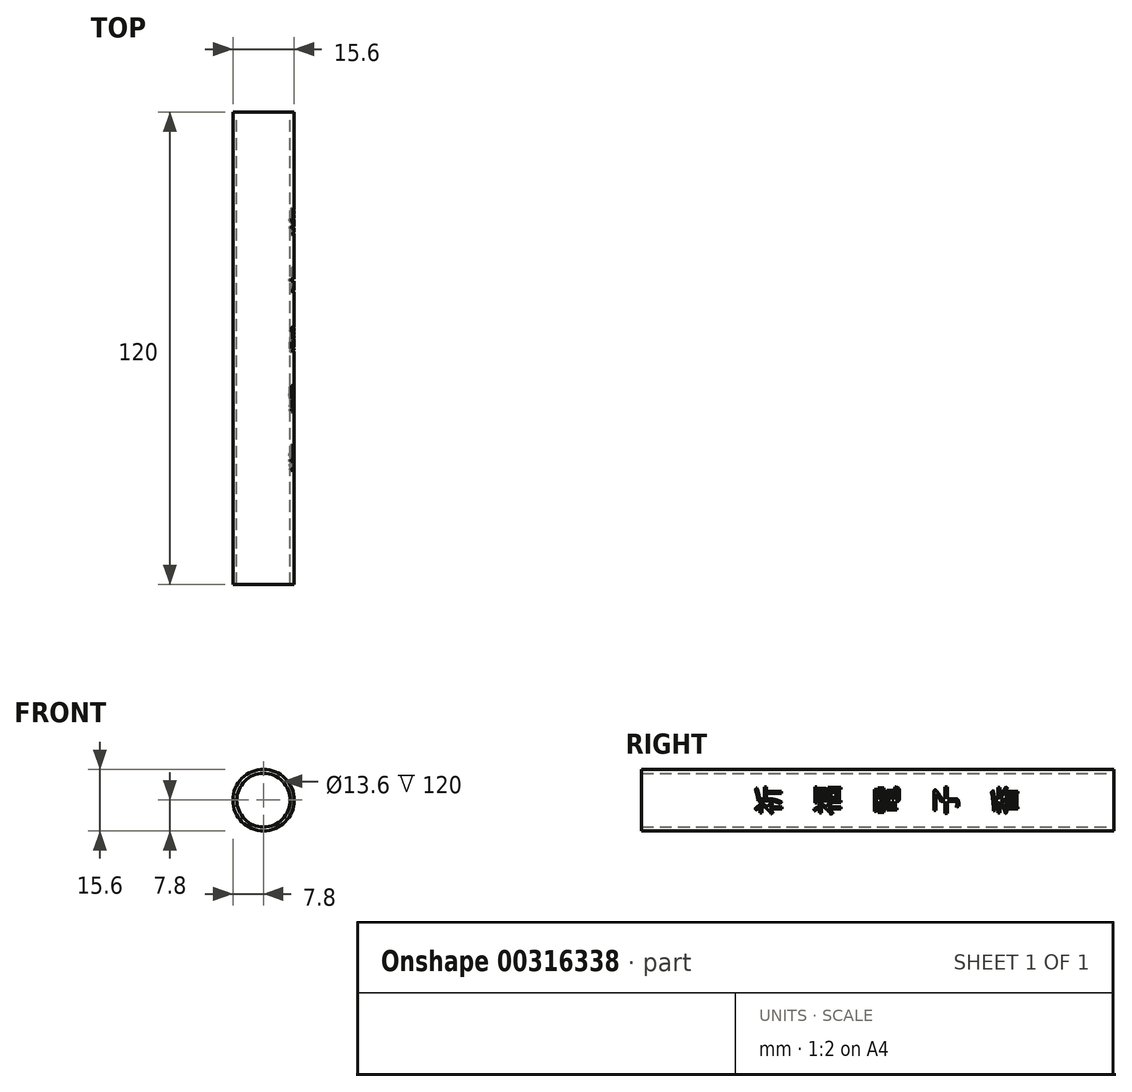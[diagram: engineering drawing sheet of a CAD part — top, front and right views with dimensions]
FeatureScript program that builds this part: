
annotation { "Feature Type Name" : "Feature", "Feature Type Description" : "" }
export const myFeature = defineFeature(function(context is Context, id is Id, definition is map)
    precondition{}
    {
        {
            var Q0;
            Q0=qCreatedBy(makeId("Front.planeOp"),FACE);
            var sketch = newSketch(context, id + "F0", { "sketchPlane" : qUnion([Q0])});
            skCircle(sketch, "E0", {"center": v(0, 0) * mm, "radius": 7.8 * mm});
            skSolve(sketch);
        }
        {
            var Q0;
            Q0 = qSketchRegion(id + "F0", true);
            extrude(context, id + "F1", {"entities" : qUnion([Q0]), "depth" : 120 * mm});
        }
        {
            var Q0;
            Q0=makeQuery(id+"F1.opExtrude","CAP_FACE",FACE,{"disambiguationData":[OSD([sQuery(id+"F0.wireOp",EDGE,"E0")])],"isStart":true});
            var sketch = newSketch(context, id + "F2", { "sketchPlane" : qUnion([Q0])});
            skCircle(sketch, "E1", {"center": v(0, 0) * mm, "radius": 6.8 * mm});
            skSolve(sketch);
        }
        {
            var Q0;
            Q0 = qSketchRegion(id + "F2", true);
            extrude(context, id + "F3", {"entities" : qUnion([Q0]), "operationType" : NewBodyOperationType.REMOVE, "oppositeDirection" : true, "depth" : 120 * mm});
        }
        {
            var Q0;
            Q0=qCreatedBy(makeId("Right.planeOp"),FACE);
            cPlane(context, id + "F4", {"entities" : qUnion([Q0]), "cplaneType" : CPlaneType.OFFSET, "offset" : 10 * mm, "width" : 150 * mm, "height" : 150 * mm});
        }
        {
            var Q0;
            Q0=qCreatedBy(id+"F4.planeOp",FACE);
            var sketch = newSketch(context, id + "F5", { "sketchPlane" : qUnion([Q0])});
            skText(sketch, "E2", { "text": "祈", "fontName": "NotoSansCJKtc-Regular.otf"});
            skText(sketch, "E3", { "text": "福", "fontName": "NotoSansCJKtc-Regular.otf"});
            skText(sketch, "E4", { "text": "電", "fontName": "NotoSansCJKtc-Regular.otf"});
            skText(sketch, "E5", { "text": "子", "fontName": "NotoSansCJKtc-Regular.otf"});
            skText(sketch, "E6", { "text": "香", "fontName": "NotoSansCJKtc-Regular.otf"});
            const initialGuessF5  = {"E2": [-0.085, -0.00375, 0, 1, 0.00534], "E3": [-0.07, -0.00375, 0, 1, 0.00543], "E4": [-0.055, -0.00375, 0, 1, 0.00532], "E5": [-0.04, -0.00375, 0, 1, 0.00537], "E6": [-0.025, -0.00375, 0, 1, 0.00536]};
            skSetInitialGuess(sketch, initialGuessF5);
            skSolve(sketch);
        }
        {
            var Q0;
            Q0 = qSketchRegion(id + "F5", true);
            var Q1;
            Q1=makeQuery(id+"F1.opExtrude","SWEPT_FACE",FACE,{"disambiguationData":[OSD([sQuery(id+"F0.wireOp",EDGE,"E0")])]});
            extrude(context, id + "F6", {"entities" : qUnion([Q0]), "endBound" : BoundingType.UP_TO_SURFACE, "oppositeDirection" : true, "endBoundEntityFace" : qUnion([Q1]), "depth" : 2 * mm});
        }
        {
            var Q0;
            Q0=makeQuery(id+"F6.opExtrude","SWEPT_BODY",BODY,{"disambiguationData":[OSD([sQuery(id+"F5.wireOp",EDGE,"E2.sketch_text.stroke-0"),sQuery(id+"F5.wireOp",EDGE,"E2.sketch_text.stroke-1"),sQuery(id+"F5.wireOp",EDGE,"E2.sketch_text.stroke-2"),sQuery(id+"F5.wireOp",EDGE,"E2.sketch_text.stroke-3")])]});
            var Q1;
            Q1=makeQuery(id+"F6.opExtrude","SWEPT_BODY",BODY,{"disambiguationData":[OSD([sQuery(id+"F5.wireOp",EDGE,"E2.sketch_text.stroke-4"),sQuery(id+"F5.wireOp",EDGE,"E2.sketch_text.stroke-5"),sQuery(id+"F5.wireOp",EDGE,"E2.sketch_text.stroke-6"),sQuery(id+"F5.wireOp",EDGE,"E2.sketch_text.stroke-7"),sQuery(id+"F5.wireOp",EDGE,"E2.sketch_text.stroke-8"),sQuery(id+"F5.wireOp",EDGE,"E2.sketch_text.stroke-9"),sQuery(id+"F5.wireOp",EDGE,"E2.sketch_text.stroke-10"),sQuery(id+"F5.wireOp",EDGE,"E2.sketch_text.stroke-11"),sQuery(id+"F5.wireOp",EDGE,"E2.sketch_text.stroke-12"),sQuery(id+"F5.wireOp",EDGE,"E2.sketch_text.stroke-13"),sQuery(id+"F5.wireOp",EDGE,"E2.sketch_text.stroke-14"),sQuery(id+"F5.wireOp",EDGE,"E2.sketch_text.stroke-15"),sQuery(id+"F5.wireOp",EDGE,"E2.sketch_text.stroke-16"),sQuery(id+"F5.wireOp",EDGE,"E2.sketch_text.stroke-17"),sQuery(id+"F5.wireOp",EDGE,"E2.sketch_text.stroke-18")])]});
            var Q2;
            Q2=makeQuery(id+"F6.opExtrude","SWEPT_BODY",BODY,{"disambiguationData":[OSD([sQuery(id+"F5.wireOp",EDGE,"E2.sketch_text.stroke-19"),sQuery(id+"F5.wireOp",EDGE,"E2.sketch_text.stroke-20"),sQuery(id+"F5.wireOp",EDGE,"E2.sketch_text.stroke-21"),sQuery(id+"F5.wireOp",EDGE,"E2.sketch_text.stroke-22"),sQuery(id+"F5.wireOp",EDGE,"E2.sketch_text.stroke-23"),sQuery(id+"F5.wireOp",EDGE,"E2.sketch_text.stroke-24"),sQuery(id+"F5.wireOp",EDGE,"E2.sketch_text.stroke-25"),sQuery(id+"F5.wireOp",EDGE,"E2.sketch_text.stroke-26"),sQuery(id+"F5.wireOp",EDGE,"E2.sketch_text.stroke-27"),sQuery(id+"F5.wireOp",EDGE,"E2.sketch_text.stroke-28"),sQuery(id+"F5.wireOp",EDGE,"E2.sketch_text.stroke-29"),sQuery(id+"F5.wireOp",EDGE,"E2.sketch_text.stroke-30"),sQuery(id+"F5.wireOp",EDGE,"E2.sketch_text.stroke-31"),sQuery(id+"F5.wireOp",EDGE,"E2.sketch_text.stroke-32"),sQuery(id+"F5.wireOp",EDGE,"E2.sketch_text.stroke-33")])]});
            transform(context, id + "F7", {"entities" : qUnion([Q0, Q1, Q2]), "transformType" : TransformType.TRANSLATION_3D, "dx" : 1 * mm, "dy" : 0 * mm, "dz" : 0 * mm, "makeCopy" : true});
        }
        {
            var Q0;
            Q0=makeQuery(id+"F7.opPattern","COPY",BODY,{"derivedFrom":makeQuery(id+"F6.opExtrude","SWEPT_BODY",BODY,{"disambiguationData":[OSD([sQuery(id+"F5.wireOp",EDGE,"E2.sketch_text.stroke-19"),sQuery(id+"F5.wireOp",EDGE,"E2.sketch_text.stroke-20"),sQuery(id+"F5.wireOp",EDGE,"E2.sketch_text.stroke-21"),sQuery(id+"F5.wireOp",EDGE,"E2.sketch_text.stroke-22"),sQuery(id+"F5.wireOp",EDGE,"E2.sketch_text.stroke-23"),sQuery(id+"F5.wireOp",EDGE,"E2.sketch_text.stroke-24"),sQuery(id+"F5.wireOp",EDGE,"E2.sketch_text.stroke-25"),sQuery(id+"F5.wireOp",EDGE,"E2.sketch_text.stroke-26"),sQuery(id+"F5.wireOp",EDGE,"E2.sketch_text.stroke-27"),sQuery(id+"F5.wireOp",EDGE,"E2.sketch_text.stroke-28"),sQuery(id+"F5.wireOp",EDGE,"E2.sketch_text.stroke-29"),sQuery(id+"F5.wireOp",EDGE,"E2.sketch_text.stroke-30"),sQuery(id+"F5.wireOp",EDGE,"E2.sketch_text.stroke-31"),sQuery(id+"F5.wireOp",EDGE,"E2.sketch_text.stroke-32"),sQuery(id+"F5.wireOp",EDGE,"E2.sketch_text.stroke-33")])]}),"instanceName":"1"});
            var Q1;
            Q1=makeQuery(id+"F7.opPattern","COPY",BODY,{"derivedFrom":makeQuery(id+"F6.opExtrude","SWEPT_BODY",BODY,{"disambiguationData":[OSD([sQuery(id+"F5.wireOp",EDGE,"E2.sketch_text.stroke-4"),sQuery(id+"F5.wireOp",EDGE,"E2.sketch_text.stroke-5"),sQuery(id+"F5.wireOp",EDGE,"E2.sketch_text.stroke-6"),sQuery(id+"F5.wireOp",EDGE,"E2.sketch_text.stroke-7"),sQuery(id+"F5.wireOp",EDGE,"E2.sketch_text.stroke-8"),sQuery(id+"F5.wireOp",EDGE,"E2.sketch_text.stroke-9"),sQuery(id+"F5.wireOp",EDGE,"E2.sketch_text.stroke-10"),sQuery(id+"F5.wireOp",EDGE,"E2.sketch_text.stroke-11"),sQuery(id+"F5.wireOp",EDGE,"E2.sketch_text.stroke-12"),sQuery(id+"F5.wireOp",EDGE,"E2.sketch_text.stroke-13"),sQuery(id+"F5.wireOp",EDGE,"E2.sketch_text.stroke-14"),sQuery(id+"F5.wireOp",EDGE,"E2.sketch_text.stroke-15"),sQuery(id+"F5.wireOp",EDGE,"E2.sketch_text.stroke-16"),sQuery(id+"F5.wireOp",EDGE,"E2.sketch_text.stroke-17"),sQuery(id+"F5.wireOp",EDGE,"E2.sketch_text.stroke-18")])]}),"instanceName":"1"});
            var Q2;
            Q2=makeQuery(id+"F7.opPattern","COPY",BODY,{"derivedFrom":makeQuery(id+"F6.opExtrude","SWEPT_BODY",BODY,{"disambiguationData":[OSD([sQuery(id+"F5.wireOp",EDGE,"E2.sketch_text.stroke-0"),sQuery(id+"F5.wireOp",EDGE,"E2.sketch_text.stroke-1"),sQuery(id+"F5.wireOp",EDGE,"E2.sketch_text.stroke-2"),sQuery(id+"F5.wireOp",EDGE,"E2.sketch_text.stroke-3")])]}),"instanceName":"1"});
            var Q3;
            Q3=makeQuery(id+"F6.opExtrude","SWEPT_BODY",BODY,{"disambiguationData":[OSD([sQuery(id+"F5.wireOp",EDGE,"E2.sketch_text.stroke-0"),sQuery(id+"F5.wireOp",EDGE,"E2.sketch_text.stroke-1"),sQuery(id+"F5.wireOp",EDGE,"E2.sketch_text.stroke-2"),sQuery(id+"F5.wireOp",EDGE,"E2.sketch_text.stroke-3")])]});
            var Q4;
            Q4=makeQuery(id+"F6.opExtrude","SWEPT_BODY",BODY,{"disambiguationData":[OSD([sQuery(id+"F5.wireOp",EDGE,"E2.sketch_text.stroke-4"),sQuery(id+"F5.wireOp",EDGE,"E2.sketch_text.stroke-5"),sQuery(id+"F5.wireOp",EDGE,"E2.sketch_text.stroke-6"),sQuery(id+"F5.wireOp",EDGE,"E2.sketch_text.stroke-7"),sQuery(id+"F5.wireOp",EDGE,"E2.sketch_text.stroke-8"),sQuery(id+"F5.wireOp",EDGE,"E2.sketch_text.stroke-9"),sQuery(id+"F5.wireOp",EDGE,"E2.sketch_text.stroke-10"),sQuery(id+"F5.wireOp",EDGE,"E2.sketch_text.stroke-11"),sQuery(id+"F5.wireOp",EDGE,"E2.sketch_text.stroke-12"),sQuery(id+"F5.wireOp",EDGE,"E2.sketch_text.stroke-13"),sQuery(id+"F5.wireOp",EDGE,"E2.sketch_text.stroke-14"),sQuery(id+"F5.wireOp",EDGE,"E2.sketch_text.stroke-15"),sQuery(id+"F5.wireOp",EDGE,"E2.sketch_text.stroke-16"),sQuery(id+"F5.wireOp",EDGE,"E2.sketch_text.stroke-17"),sQuery(id+"F5.wireOp",EDGE,"E2.sketch_text.stroke-18")])]});
            var Q5;
            Q5=makeQuery(id+"F6.opExtrude","SWEPT_BODY",BODY,{"disambiguationData":[OSD([sQuery(id+"F5.wireOp",EDGE,"E2.sketch_text.stroke-19"),sQuery(id+"F5.wireOp",EDGE,"E2.sketch_text.stroke-20"),sQuery(id+"F5.wireOp",EDGE,"E2.sketch_text.stroke-21"),sQuery(id+"F5.wireOp",EDGE,"E2.sketch_text.stroke-22"),sQuery(id+"F5.wireOp",EDGE,"E2.sketch_text.stroke-23"),sQuery(id+"F5.wireOp",EDGE,"E2.sketch_text.stroke-24"),sQuery(id+"F5.wireOp",EDGE,"E2.sketch_text.stroke-25"),sQuery(id+"F5.wireOp",EDGE,"E2.sketch_text.stroke-26"),sQuery(id+"F5.wireOp",EDGE,"E2.sketch_text.stroke-27"),sQuery(id+"F5.wireOp",EDGE,"E2.sketch_text.stroke-28"),sQuery(id+"F5.wireOp",EDGE,"E2.sketch_text.stroke-29"),sQuery(id+"F5.wireOp",EDGE,"E2.sketch_text.stroke-30"),sQuery(id+"F5.wireOp",EDGE,"E2.sketch_text.stroke-31"),sQuery(id+"F5.wireOp",EDGE,"E2.sketch_text.stroke-32"),sQuery(id+"F5.wireOp",EDGE,"E2.sketch_text.stroke-33")])]});
            booleanBodies(context, id + "F8", {"operationType" : BooleanOperationType.SUBTRACTION, "tools" : qUnion([Q0, Q1, Q2]), "targets" : qUnion([Q3, Q4, Q5])});
        }
        {
            var Q0;
            Q0=makeQuery(id+"F6.opExtrude","SWEPT_BODY",BODY,{"disambiguationData":[OSD([sQuery(id+"F5.wireOp",EDGE,"E3.sketch_text.stroke-0"),sQuery(id+"F5.wireOp",EDGE,"E3.sketch_text.stroke-1"),sQuery(id+"F5.wireOp",EDGE,"E3.sketch_text.stroke-2"),sQuery(id+"F5.wireOp",EDGE,"E3.sketch_text.stroke-3")])]});
            var Q1;
            Q1=makeQuery(id+"F6.opExtrude","SWEPT_BODY",BODY,{"disambiguationData":[OSD([sQuery(id+"F5.wireOp",EDGE,"E3.sketch_text.stroke-4"),sQuery(id+"F5.wireOp",EDGE,"E3.sketch_text.stroke-5"),sQuery(id+"F5.wireOp",EDGE,"E3.sketch_text.stroke-6"),sQuery(id+"F5.wireOp",EDGE,"E3.sketch_text.stroke-7"),sQuery(id+"F5.wireOp",EDGE,"E3.sketch_text.stroke-8"),sQuery(id+"F5.wireOp",EDGE,"E3.sketch_text.stroke-9"),sQuery(id+"F5.wireOp",EDGE,"E3.sketch_text.stroke-10"),sQuery(id+"F5.wireOp",EDGE,"E3.sketch_text.stroke-11"),sQuery(id+"F5.wireOp",EDGE,"E3.sketch_text.stroke-12"),sQuery(id+"F5.wireOp",EDGE,"E3.sketch_text.stroke-13"),sQuery(id+"F5.wireOp",EDGE,"E3.sketch_text.stroke-14"),sQuery(id+"F5.wireOp",EDGE,"E3.sketch_text.stroke-15"),sQuery(id+"F5.wireOp",EDGE,"E3.sketch_text.stroke-16"),sQuery(id+"F5.wireOp",EDGE,"E3.sketch_text.stroke-17"),sQuery(id+"F5.wireOp",EDGE,"E3.sketch_text.stroke-18"),sQuery(id+"F5.wireOp",EDGE,"E3.sketch_text.stroke-19"),sQuery(id+"F5.wireOp",EDGE,"E3.sketch_text.stroke-20"),sQuery(id+"F5.wireOp",EDGE,"E3.sketch_text.stroke-21"),sQuery(id+"F5.wireOp",EDGE,"E3.sketch_text.stroke-22"),sQuery(id+"F5.wireOp",EDGE,"E3.sketch_text.stroke-23"),sQuery(id+"F5.wireOp",EDGE,"E3.sketch_text.stroke-24"),sQuery(id+"F5.wireOp",EDGE,"E3.sketch_text.stroke-25"),sQuery(id+"F5.wireOp",EDGE,"E3.sketch_text.stroke-26"),sQuery(id+"F5.wireOp",EDGE,"E3.sketch_text.stroke-27"),sQuery(id+"F5.wireOp",EDGE,"E3.sketch_text.stroke-28"),sQuery(id+"F5.wireOp",EDGE,"E3.sketch_text.stroke-29"),sQuery(id+"F5.wireOp",EDGE,"E3.sketch_text.stroke-30"),sQuery(id+"F5.wireOp",EDGE,"E3.sketch_text.stroke-31"),sQuery(id+"F5.wireOp",EDGE,"E3.sketch_text.stroke-32"),sQuery(id+"F5.wireOp",EDGE,"E3.sketch_text.stroke-33"),sQuery(id+"F5.wireOp",EDGE,"E3.sketch_text.stroke-34"),sQuery(id+"F5.wireOp",EDGE,"E3.sketch_text.stroke-35"),sQuery(id+"F5.wireOp",EDGE,"E3.sketch_text.stroke-36"),sQuery(id+"F5.wireOp",EDGE,"E3.sketch_text.stroke-37"),sQuery(id+"F5.wireOp",EDGE,"E3.sketch_text.stroke-38"),sQuery(id+"F5.wireOp",EDGE,"E3.sketch_text.stroke-39"),sQuery(id+"F5.wireOp",EDGE,"E3.sketch_text.stroke-40"),sQuery(id+"F5.wireOp",EDGE,"E3.sketch_text.stroke-41"),sQuery(id+"F5.wireOp",EDGE,"E3.sketch_text.stroke-42"),sQuery(id+"F5.wireOp",EDGE,"E3.sketch_text.stroke-43")])]});
            var Q2;
            Q2=makeQuery(id+"F6.opExtrude","SWEPT_BODY",BODY,{"disambiguationData":[OSD([sQuery(id+"F5.wireOp",EDGE,"E3.sketch_text.stroke-44"),sQuery(id+"F5.wireOp",EDGE,"E3.sketch_text.stroke-45"),sQuery(id+"F5.wireOp",EDGE,"E3.sketch_text.stroke-46"),sQuery(id+"F5.wireOp",EDGE,"E3.sketch_text.stroke-47"),sQuery(id+"F5.wireOp",EDGE,"E3.sketch_text.stroke-48"),sQuery(id+"F5.wireOp",EDGE,"E3.sketch_text.stroke-49"),sQuery(id+"F5.wireOp",EDGE,"E3.sketch_text.stroke-50"),sQuery(id+"F5.wireOp",EDGE,"E3.sketch_text.stroke-51")])]});
            var Q3;
            Q3=makeQuery(id+"F6.opExtrude","SWEPT_BODY",BODY,{"disambiguationData":[OSD([sQuery(id+"F5.wireOp",EDGE,"E3.sketch_text.stroke-52"),sQuery(id+"F5.wireOp",EDGE,"E3.sketch_text.stroke-53"),sQuery(id+"F5.wireOp",EDGE,"E3.sketch_text.stroke-54"),sQuery(id+"F5.wireOp",EDGE,"E3.sketch_text.stroke-55")])]});
            transform(context, id + "F9", {"entities" : qUnion([Q0, Q1, Q2, Q3]), "transformType" : TransformType.TRANSLATION_3D, "dx" : 1 * mm, "dy" : 0 * mm, "dz" : 0 * mm, "makeCopy" : true});
        }
        {
            var Q0;
            Q0=makeQuery(id+"F9.opPattern","COPY",BODY,{"derivedFrom":makeQuery(id+"F6.opExtrude","SWEPT_BODY",BODY,{"disambiguationData":[OSD([sQuery(id+"F5.wireOp",EDGE,"E3.sketch_text.stroke-52"),sQuery(id+"F5.wireOp",EDGE,"E3.sketch_text.stroke-53"),sQuery(id+"F5.wireOp",EDGE,"E3.sketch_text.stroke-54"),sQuery(id+"F5.wireOp",EDGE,"E3.sketch_text.stroke-55")])]}),"instanceName":"1"});
            var Q1;
            Q1=makeQuery(id+"F9.opPattern","COPY",BODY,{"derivedFrom":makeQuery(id+"F6.opExtrude","SWEPT_BODY",BODY,{"disambiguationData":[OSD([sQuery(id+"F5.wireOp",EDGE,"E3.sketch_text.stroke-44"),sQuery(id+"F5.wireOp",EDGE,"E3.sketch_text.stroke-45"),sQuery(id+"F5.wireOp",EDGE,"E3.sketch_text.stroke-46"),sQuery(id+"F5.wireOp",EDGE,"E3.sketch_text.stroke-47"),sQuery(id+"F5.wireOp",EDGE,"E3.sketch_text.stroke-48"),sQuery(id+"F5.wireOp",EDGE,"E3.sketch_text.stroke-49"),sQuery(id+"F5.wireOp",EDGE,"E3.sketch_text.stroke-50"),sQuery(id+"F5.wireOp",EDGE,"E3.sketch_text.stroke-51")])]}),"instanceName":"1"});
            var Q2;
            Q2=makeQuery(id+"F9.opPattern","COPY",BODY,{"derivedFrom":makeQuery(id+"F6.opExtrude","SWEPT_BODY",BODY,{"disambiguationData":[OSD([sQuery(id+"F5.wireOp",EDGE,"E3.sketch_text.stroke-4"),sQuery(id+"F5.wireOp",EDGE,"E3.sketch_text.stroke-5"),sQuery(id+"F5.wireOp",EDGE,"E3.sketch_text.stroke-6"),sQuery(id+"F5.wireOp",EDGE,"E3.sketch_text.stroke-7"),sQuery(id+"F5.wireOp",EDGE,"E3.sketch_text.stroke-8"),sQuery(id+"F5.wireOp",EDGE,"E3.sketch_text.stroke-9"),sQuery(id+"F5.wireOp",EDGE,"E3.sketch_text.stroke-10"),sQuery(id+"F5.wireOp",EDGE,"E3.sketch_text.stroke-11"),sQuery(id+"F5.wireOp",EDGE,"E3.sketch_text.stroke-12"),sQuery(id+"F5.wireOp",EDGE,"E3.sketch_text.stroke-13"),sQuery(id+"F5.wireOp",EDGE,"E3.sketch_text.stroke-14"),sQuery(id+"F5.wireOp",EDGE,"E3.sketch_text.stroke-15"),sQuery(id+"F5.wireOp",EDGE,"E3.sketch_text.stroke-16"),sQuery(id+"F5.wireOp",EDGE,"E3.sketch_text.stroke-17"),sQuery(id+"F5.wireOp",EDGE,"E3.sketch_text.stroke-18"),sQuery(id+"F5.wireOp",EDGE,"E3.sketch_text.stroke-19"),sQuery(id+"F5.wireOp",EDGE,"E3.sketch_text.stroke-20"),sQuery(id+"F5.wireOp",EDGE,"E3.sketch_text.stroke-21"),sQuery(id+"F5.wireOp",EDGE,"E3.sketch_text.stroke-22"),sQuery(id+"F5.wireOp",EDGE,"E3.sketch_text.stroke-23"),sQuery(id+"F5.wireOp",EDGE,"E3.sketch_text.stroke-24"),sQuery(id+"F5.wireOp",EDGE,"E3.sketch_text.stroke-25"),sQuery(id+"F5.wireOp",EDGE,"E3.sketch_text.stroke-26"),sQuery(id+"F5.wireOp",EDGE,"E3.sketch_text.stroke-27"),sQuery(id+"F5.wireOp",EDGE,"E3.sketch_text.stroke-28"),sQuery(id+"F5.wireOp",EDGE,"E3.sketch_text.stroke-29"),sQuery(id+"F5.wireOp",EDGE,"E3.sketch_text.stroke-30"),sQuery(id+"F5.wireOp",EDGE,"E3.sketch_text.stroke-31"),sQuery(id+"F5.wireOp",EDGE,"E3.sketch_text.stroke-32"),sQuery(id+"F5.wireOp",EDGE,"E3.sketch_text.stroke-33"),sQuery(id+"F5.wireOp",EDGE,"E3.sketch_text.stroke-34"),sQuery(id+"F5.wireOp",EDGE,"E3.sketch_text.stroke-35"),sQuery(id+"F5.wireOp",EDGE,"E3.sketch_text.stroke-36"),sQuery(id+"F5.wireOp",EDGE,"E3.sketch_text.stroke-37"),sQuery(id+"F5.wireOp",EDGE,"E3.sketch_text.stroke-38"),sQuery(id+"F5.wireOp",EDGE,"E3.sketch_text.stroke-39"),sQuery(id+"F5.wireOp",EDGE,"E3.sketch_text.stroke-40"),sQuery(id+"F5.wireOp",EDGE,"E3.sketch_text.stroke-41"),sQuery(id+"F5.wireOp",EDGE,"E3.sketch_text.stroke-42"),sQuery(id+"F5.wireOp",EDGE,"E3.sketch_text.stroke-43")])]}),"instanceName":"1"});
            var Q3;
            Q3=makeQuery(id+"F9.opPattern","COPY",BODY,{"derivedFrom":makeQuery(id+"F6.opExtrude","SWEPT_BODY",BODY,{"disambiguationData":[OSD([sQuery(id+"F5.wireOp",EDGE,"E3.sketch_text.stroke-0"),sQuery(id+"F5.wireOp",EDGE,"E3.sketch_text.stroke-1"),sQuery(id+"F5.wireOp",EDGE,"E3.sketch_text.stroke-2"),sQuery(id+"F5.wireOp",EDGE,"E3.sketch_text.stroke-3")])]}),"instanceName":"1"});
            var Q4;
            Q4=makeQuery(id+"F6.opExtrude","SWEPT_BODY",BODY,{"disambiguationData":[OSD([sQuery(id+"F5.wireOp",EDGE,"E3.sketch_text.stroke-0"),sQuery(id+"F5.wireOp",EDGE,"E3.sketch_text.stroke-1"),sQuery(id+"F5.wireOp",EDGE,"E3.sketch_text.stroke-2"),sQuery(id+"F5.wireOp",EDGE,"E3.sketch_text.stroke-3")])]});
            var Q5;
            Q5=makeQuery(id+"F6.opExtrude","SWEPT_BODY",BODY,{"disambiguationData":[OSD([sQuery(id+"F5.wireOp",EDGE,"E3.sketch_text.stroke-4"),sQuery(id+"F5.wireOp",EDGE,"E3.sketch_text.stroke-5"),sQuery(id+"F5.wireOp",EDGE,"E3.sketch_text.stroke-6"),sQuery(id+"F5.wireOp",EDGE,"E3.sketch_text.stroke-7"),sQuery(id+"F5.wireOp",EDGE,"E3.sketch_text.stroke-8"),sQuery(id+"F5.wireOp",EDGE,"E3.sketch_text.stroke-9"),sQuery(id+"F5.wireOp",EDGE,"E3.sketch_text.stroke-10"),sQuery(id+"F5.wireOp",EDGE,"E3.sketch_text.stroke-11"),sQuery(id+"F5.wireOp",EDGE,"E3.sketch_text.stroke-12"),sQuery(id+"F5.wireOp",EDGE,"E3.sketch_text.stroke-13"),sQuery(id+"F5.wireOp",EDGE,"E3.sketch_text.stroke-14"),sQuery(id+"F5.wireOp",EDGE,"E3.sketch_text.stroke-15"),sQuery(id+"F5.wireOp",EDGE,"E3.sketch_text.stroke-16"),sQuery(id+"F5.wireOp",EDGE,"E3.sketch_text.stroke-17"),sQuery(id+"F5.wireOp",EDGE,"E3.sketch_text.stroke-18"),sQuery(id+"F5.wireOp",EDGE,"E3.sketch_text.stroke-19"),sQuery(id+"F5.wireOp",EDGE,"E3.sketch_text.stroke-20"),sQuery(id+"F5.wireOp",EDGE,"E3.sketch_text.stroke-21"),sQuery(id+"F5.wireOp",EDGE,"E3.sketch_text.stroke-22"),sQuery(id+"F5.wireOp",EDGE,"E3.sketch_text.stroke-23"),sQuery(id+"F5.wireOp",EDGE,"E3.sketch_text.stroke-24"),sQuery(id+"F5.wireOp",EDGE,"E3.sketch_text.stroke-25"),sQuery(id+"F5.wireOp",EDGE,"E3.sketch_text.stroke-26"),sQuery(id+"F5.wireOp",EDGE,"E3.sketch_text.stroke-27"),sQuery(id+"F5.wireOp",EDGE,"E3.sketch_text.stroke-28"),sQuery(id+"F5.wireOp",EDGE,"E3.sketch_text.stroke-29"),sQuery(id+"F5.wireOp",EDGE,"E3.sketch_text.stroke-30"),sQuery(id+"F5.wireOp",EDGE,"E3.sketch_text.stroke-31"),sQuery(id+"F5.wireOp",EDGE,"E3.sketch_text.stroke-32"),sQuery(id+"F5.wireOp",EDGE,"E3.sketch_text.stroke-33"),sQuery(id+"F5.wireOp",EDGE,"E3.sketch_text.stroke-34"),sQuery(id+"F5.wireOp",EDGE,"E3.sketch_text.stroke-35"),sQuery(id+"F5.wireOp",EDGE,"E3.sketch_text.stroke-36"),sQuery(id+"F5.wireOp",EDGE,"E3.sketch_text.stroke-37"),sQuery(id+"F5.wireOp",EDGE,"E3.sketch_text.stroke-38"),sQuery(id+"F5.wireOp",EDGE,"E3.sketch_text.stroke-39"),sQuery(id+"F5.wireOp",EDGE,"E3.sketch_text.stroke-40"),sQuery(id+"F5.wireOp",EDGE,"E3.sketch_text.stroke-41"),sQuery(id+"F5.wireOp",EDGE,"E3.sketch_text.stroke-42"),sQuery(id+"F5.wireOp",EDGE,"E3.sketch_text.stroke-43")])]});
            var Q6;
            Q6=makeQuery(id+"F6.opExtrude","SWEPT_BODY",BODY,{"disambiguationData":[OSD([sQuery(id+"F5.wireOp",EDGE,"E3.sketch_text.stroke-44"),sQuery(id+"F5.wireOp",EDGE,"E3.sketch_text.stroke-45"),sQuery(id+"F5.wireOp",EDGE,"E3.sketch_text.stroke-46"),sQuery(id+"F5.wireOp",EDGE,"E3.sketch_text.stroke-47"),sQuery(id+"F5.wireOp",EDGE,"E3.sketch_text.stroke-48"),sQuery(id+"F5.wireOp",EDGE,"E3.sketch_text.stroke-49"),sQuery(id+"F5.wireOp",EDGE,"E3.sketch_text.stroke-50"),sQuery(id+"F5.wireOp",EDGE,"E3.sketch_text.stroke-51")])]});
            var Q7;
            Q7=makeQuery(id+"F6.opExtrude","SWEPT_BODY",BODY,{"disambiguationData":[OSD([sQuery(id+"F5.wireOp",EDGE,"E3.sketch_text.stroke-52"),sQuery(id+"F5.wireOp",EDGE,"E3.sketch_text.stroke-53"),sQuery(id+"F5.wireOp",EDGE,"E3.sketch_text.stroke-54"),sQuery(id+"F5.wireOp",EDGE,"E3.sketch_text.stroke-55")])]});
            booleanBodies(context, id + "F10", {"operationType" : BooleanOperationType.SUBTRACTION, "tools" : qUnion([Q0, Q1, Q2, Q3]), "targets" : qUnion([Q4, Q5, Q6, Q7])});
        }
        {
            var Q0;
            Q0=makeQuery(id+"F6.opExtrude","SWEPT_BODY",BODY,{"disambiguationData":[OSD([sQuery(id+"F5.wireOp",EDGE,"E4.sketch_text.stroke-0"),sQuery(id+"F5.wireOp",EDGE,"E4.sketch_text.stroke-1"),sQuery(id+"F5.wireOp",EDGE,"E4.sketch_text.stroke-2"),sQuery(id+"F5.wireOp",EDGE,"E4.sketch_text.stroke-3"),sQuery(id+"F5.wireOp",EDGE,"E4.sketch_text.stroke-4"),sQuery(id+"F5.wireOp",EDGE,"E4.sketch_text.stroke-5"),sQuery(id+"F5.wireOp",EDGE,"E4.sketch_text.stroke-6"),sQuery(id+"F5.wireOp",EDGE,"E4.sketch_text.stroke-7"),sQuery(id+"F5.wireOp",EDGE,"E4.sketch_text.stroke-8"),sQuery(id+"F5.wireOp",EDGE,"E4.sketch_text.stroke-9"),sQuery(id+"F5.wireOp",EDGE,"E4.sketch_text.stroke-10"),sQuery(id+"F5.wireOp",EDGE,"E4.sketch_text.stroke-11"),sQuery(id+"F5.wireOp",EDGE,"E4.sketch_text.stroke-12"),sQuery(id+"F5.wireOp",EDGE,"E4.sketch_text.stroke-13"),sQuery(id+"F5.wireOp",EDGE,"E4.sketch_text.stroke-14"),sQuery(id+"F5.wireOp",EDGE,"E4.sketch_text.stroke-15"),sQuery(id+"F5.wireOp",EDGE,"E4.sketch_text.stroke-16"),sQuery(id+"F5.wireOp",EDGE,"E4.sketch_text.stroke-17"),sQuery(id+"F5.wireOp",EDGE,"E4.sketch_text.stroke-18"),sQuery(id+"F5.wireOp",EDGE,"E4.sketch_text.stroke-19")])]});
            var Q1;
            Q1=makeQuery(id+"F6.opExtrude","SWEPT_BODY",BODY,{"disambiguationData":[OSD([sQuery(id+"F5.wireOp",EDGE,"E4.sketch_text.stroke-20"),sQuery(id+"F5.wireOp",EDGE,"E4.sketch_text.stroke-21"),sQuery(id+"F5.wireOp",EDGE,"E4.sketch_text.stroke-22"),sQuery(id+"F5.wireOp",EDGE,"E4.sketch_text.stroke-23")])]});
            var Q2;
            Q2=makeQuery(id+"F6.opExtrude","SWEPT_BODY",BODY,{"disambiguationData":[OSD([sQuery(id+"F5.wireOp",EDGE,"E4.sketch_text.stroke-24"),sQuery(id+"F5.wireOp",EDGE,"E4.sketch_text.stroke-25"),sQuery(id+"F5.wireOp",EDGE,"E4.sketch_text.stroke-26"),sQuery(id+"F5.wireOp",EDGE,"E4.sketch_text.stroke-27")])]});
            var Q3;
            Q3=makeQuery(id+"F6.opExtrude","SWEPT_BODY",BODY,{"disambiguationData":[OSD([sQuery(id+"F5.wireOp",EDGE,"E4.sketch_text.stroke-28"),sQuery(id+"F5.wireOp",EDGE,"E4.sketch_text.stroke-29"),sQuery(id+"F5.wireOp",EDGE,"E4.sketch_text.stroke-30"),sQuery(id+"F5.wireOp",EDGE,"E4.sketch_text.stroke-31")])]});
            var Q4;
            Q4=makeQuery(id+"F6.opExtrude","SWEPT_BODY",BODY,{"disambiguationData":[OSD([sQuery(id+"F5.wireOp",EDGE,"E4.sketch_text.stroke-32"),sQuery(id+"F5.wireOp",EDGE,"E4.sketch_text.stroke-33"),sQuery(id+"F5.wireOp",EDGE,"E4.sketch_text.stroke-34"),sQuery(id+"F5.wireOp",EDGE,"E4.sketch_text.stroke-35")])]});
            var Q5;
            Q5=makeQuery(id+"F6.opExtrude","SWEPT_BODY",BODY,{"disambiguationData":[OSD([sQuery(id+"F5.wireOp",EDGE,"E4.sketch_text.stroke-36"),sQuery(id+"F5.wireOp",EDGE,"E4.sketch_text.stroke-37"),sQuery(id+"F5.wireOp",EDGE,"E4.sketch_text.stroke-38"),sQuery(id+"F5.wireOp",EDGE,"E4.sketch_text.stroke-39"),sQuery(id+"F5.wireOp",EDGE,"E4.sketch_text.stroke-40"),sQuery(id+"F5.wireOp",EDGE,"E4.sketch_text.stroke-41"),sQuery(id+"F5.wireOp",EDGE,"E4.sketch_text.stroke-42"),sQuery(id+"F5.wireOp",EDGE,"E4.sketch_text.stroke-43"),sQuery(id+"F5.wireOp",EDGE,"E4.sketch_text.stroke-44"),sQuery(id+"F5.wireOp",EDGE,"E4.sketch_text.stroke-45"),sQuery(id+"F5.wireOp",EDGE,"E4.sketch_text.stroke-46"),sQuery(id+"F5.wireOp",EDGE,"E4.sketch_text.stroke-47"),sQuery(id+"F5.wireOp",EDGE,"E4.sketch_text.stroke-48"),sQuery(id+"F5.wireOp",EDGE,"E4.sketch_text.stroke-49"),sQuery(id+"F5.wireOp",EDGE,"E4.sketch_text.stroke-50"),sQuery(id+"F5.wireOp",EDGE,"E4.sketch_text.stroke-51"),sQuery(id+"F5.wireOp",EDGE,"E4.sketch_text.stroke-52"),sQuery(id+"F5.wireOp",EDGE,"E4.sketch_text.stroke-53"),sQuery(id+"F5.wireOp",EDGE,"E4.sketch_text.stroke-54"),sQuery(id+"F5.wireOp",EDGE,"E4.sketch_text.stroke-55"),sQuery(id+"F5.wireOp",EDGE,"E4.sketch_text.stroke-56"),sQuery(id+"F5.wireOp",EDGE,"E4.sketch_text.stroke-57"),sQuery(id+"F5.wireOp",EDGE,"E4.sketch_text.stroke-58"),sQuery(id+"F5.wireOp",EDGE,"E4.sketch_text.stroke-59"),sQuery(id+"F5.wireOp",EDGE,"E4.sketch_text.stroke-60"),sQuery(id+"F5.wireOp",EDGE,"E4.sketch_text.stroke-61"),sQuery(id+"F5.wireOp",EDGE,"E4.sketch_text.stroke-62"),sQuery(id+"F5.wireOp",EDGE,"E4.sketch_text.stroke-63"),sQuery(id+"F5.wireOp",EDGE,"E4.sketch_text.stroke-64"),sQuery(id+"F5.wireOp",EDGE,"E4.sketch_text.stroke-65"),sQuery(id+"F5.wireOp",EDGE,"E4.sketch_text.stroke-66"),sQuery(id+"F5.wireOp",EDGE,"E4.sketch_text.stroke-67")])]});
            transform(context, id + "F11", {"entities" : qUnion([Q0, Q1, Q2, Q3, Q4, Q5]), "transformType" : TransformType.TRANSLATION_3D, "dx" : 1 * mm, "dy" : 0 * mm, "dz" : 0 * mm, "makeCopy" : true});
        }
        {
            var Q0;
            Q0=makeQuery(id+"F11.opPattern","COPY",BODY,{"derivedFrom":makeQuery(id+"F6.opExtrude","SWEPT_BODY",BODY,{"disambiguationData":[OSD([sQuery(id+"F5.wireOp",EDGE,"E4.sketch_text.stroke-36"),sQuery(id+"F5.wireOp",EDGE,"E4.sketch_text.stroke-37"),sQuery(id+"F5.wireOp",EDGE,"E4.sketch_text.stroke-38"),sQuery(id+"F5.wireOp",EDGE,"E4.sketch_text.stroke-39"),sQuery(id+"F5.wireOp",EDGE,"E4.sketch_text.stroke-40"),sQuery(id+"F5.wireOp",EDGE,"E4.sketch_text.stroke-41"),sQuery(id+"F5.wireOp",EDGE,"E4.sketch_text.stroke-42"),sQuery(id+"F5.wireOp",EDGE,"E4.sketch_text.stroke-43"),sQuery(id+"F5.wireOp",EDGE,"E4.sketch_text.stroke-44"),sQuery(id+"F5.wireOp",EDGE,"E4.sketch_text.stroke-45"),sQuery(id+"F5.wireOp",EDGE,"E4.sketch_text.stroke-46"),sQuery(id+"F5.wireOp",EDGE,"E4.sketch_text.stroke-47"),sQuery(id+"F5.wireOp",EDGE,"E4.sketch_text.stroke-48"),sQuery(id+"F5.wireOp",EDGE,"E4.sketch_text.stroke-49"),sQuery(id+"F5.wireOp",EDGE,"E4.sketch_text.stroke-50"),sQuery(id+"F5.wireOp",EDGE,"E4.sketch_text.stroke-51"),sQuery(id+"F5.wireOp",EDGE,"E4.sketch_text.stroke-52"),sQuery(id+"F5.wireOp",EDGE,"E4.sketch_text.stroke-53"),sQuery(id+"F5.wireOp",EDGE,"E4.sketch_text.stroke-54"),sQuery(id+"F5.wireOp",EDGE,"E4.sketch_text.stroke-55"),sQuery(id+"F5.wireOp",EDGE,"E4.sketch_text.stroke-56"),sQuery(id+"F5.wireOp",EDGE,"E4.sketch_text.stroke-57"),sQuery(id+"F5.wireOp",EDGE,"E4.sketch_text.stroke-58"),sQuery(id+"F5.wireOp",EDGE,"E4.sketch_text.stroke-59"),sQuery(id+"F5.wireOp",EDGE,"E4.sketch_text.stroke-60"),sQuery(id+"F5.wireOp",EDGE,"E4.sketch_text.stroke-61"),sQuery(id+"F5.wireOp",EDGE,"E4.sketch_text.stroke-62"),sQuery(id+"F5.wireOp",EDGE,"E4.sketch_text.stroke-63"),sQuery(id+"F5.wireOp",EDGE,"E4.sketch_text.stroke-64"),sQuery(id+"F5.wireOp",EDGE,"E4.sketch_text.stroke-65"),sQuery(id+"F5.wireOp",EDGE,"E4.sketch_text.stroke-66"),sQuery(id+"F5.wireOp",EDGE,"E4.sketch_text.stroke-67")])]}),"instanceName":"1"});
            var Q1;
            Q1=makeQuery(id+"F11.opPattern","COPY",BODY,{"derivedFrom":makeQuery(id+"F6.opExtrude","SWEPT_BODY",BODY,{"disambiguationData":[OSD([sQuery(id+"F5.wireOp",EDGE,"E4.sketch_text.stroke-32"),sQuery(id+"F5.wireOp",EDGE,"E4.sketch_text.stroke-33"),sQuery(id+"F5.wireOp",EDGE,"E4.sketch_text.stroke-34"),sQuery(id+"F5.wireOp",EDGE,"E4.sketch_text.stroke-35")])]}),"instanceName":"1"});
            var Q2;
            Q2=makeQuery(id+"F11.opPattern","COPY",BODY,{"derivedFrom":makeQuery(id+"F6.opExtrude","SWEPT_BODY",BODY,{"disambiguationData":[OSD([sQuery(id+"F5.wireOp",EDGE,"E4.sketch_text.stroke-28"),sQuery(id+"F5.wireOp",EDGE,"E4.sketch_text.stroke-29"),sQuery(id+"F5.wireOp",EDGE,"E4.sketch_text.stroke-30"),sQuery(id+"F5.wireOp",EDGE,"E4.sketch_text.stroke-31")])]}),"instanceName":"1"});
            var Q3;
            Q3=makeQuery(id+"F11.opPattern","COPY",BODY,{"derivedFrom":makeQuery(id+"F6.opExtrude","SWEPT_BODY",BODY,{"disambiguationData":[OSD([sQuery(id+"F5.wireOp",EDGE,"E4.sketch_text.stroke-24"),sQuery(id+"F5.wireOp",EDGE,"E4.sketch_text.stroke-25"),sQuery(id+"F5.wireOp",EDGE,"E4.sketch_text.stroke-26"),sQuery(id+"F5.wireOp",EDGE,"E4.sketch_text.stroke-27")])]}),"instanceName":"1"});
            var Q4;
            Q4=makeQuery(id+"F11.opPattern","COPY",BODY,{"derivedFrom":makeQuery(id+"F6.opExtrude","SWEPT_BODY",BODY,{"disambiguationData":[OSD([sQuery(id+"F5.wireOp",EDGE,"E4.sketch_text.stroke-20"),sQuery(id+"F5.wireOp",EDGE,"E4.sketch_text.stroke-21"),sQuery(id+"F5.wireOp",EDGE,"E4.sketch_text.stroke-22"),sQuery(id+"F5.wireOp",EDGE,"E4.sketch_text.stroke-23")])]}),"instanceName":"1"});
            var Q5;
            Q5=makeQuery(id+"F11.opPattern","COPY",BODY,{"derivedFrom":makeQuery(id+"F6.opExtrude","SWEPT_BODY",BODY,{"disambiguationData":[OSD([sQuery(id+"F5.wireOp",EDGE,"E4.sketch_text.stroke-0"),sQuery(id+"F5.wireOp",EDGE,"E4.sketch_text.stroke-1"),sQuery(id+"F5.wireOp",EDGE,"E4.sketch_text.stroke-2"),sQuery(id+"F5.wireOp",EDGE,"E4.sketch_text.stroke-3"),sQuery(id+"F5.wireOp",EDGE,"E4.sketch_text.stroke-4"),sQuery(id+"F5.wireOp",EDGE,"E4.sketch_text.stroke-5"),sQuery(id+"F5.wireOp",EDGE,"E4.sketch_text.stroke-6"),sQuery(id+"F5.wireOp",EDGE,"E4.sketch_text.stroke-7"),sQuery(id+"F5.wireOp",EDGE,"E4.sketch_text.stroke-8"),sQuery(id+"F5.wireOp",EDGE,"E4.sketch_text.stroke-9"),sQuery(id+"F5.wireOp",EDGE,"E4.sketch_text.stroke-10"),sQuery(id+"F5.wireOp",EDGE,"E4.sketch_text.stroke-11"),sQuery(id+"F5.wireOp",EDGE,"E4.sketch_text.stroke-12"),sQuery(id+"F5.wireOp",EDGE,"E4.sketch_text.stroke-13"),sQuery(id+"F5.wireOp",EDGE,"E4.sketch_text.stroke-14"),sQuery(id+"F5.wireOp",EDGE,"E4.sketch_text.stroke-15"),sQuery(id+"F5.wireOp",EDGE,"E4.sketch_text.stroke-16"),sQuery(id+"F5.wireOp",EDGE,"E4.sketch_text.stroke-17"),sQuery(id+"F5.wireOp",EDGE,"E4.sketch_text.stroke-18"),sQuery(id+"F5.wireOp",EDGE,"E4.sketch_text.stroke-19")])]}),"instanceName":"1"});
            var Q6;
            Q6=makeQuery(id+"F6.opExtrude","SWEPT_BODY",BODY,{"disambiguationData":[OSD([sQuery(id+"F5.wireOp",EDGE,"E4.sketch_text.stroke-0"),sQuery(id+"F5.wireOp",EDGE,"E4.sketch_text.stroke-1"),sQuery(id+"F5.wireOp",EDGE,"E4.sketch_text.stroke-2"),sQuery(id+"F5.wireOp",EDGE,"E4.sketch_text.stroke-3"),sQuery(id+"F5.wireOp",EDGE,"E4.sketch_text.stroke-4"),sQuery(id+"F5.wireOp",EDGE,"E4.sketch_text.stroke-5"),sQuery(id+"F5.wireOp",EDGE,"E4.sketch_text.stroke-6"),sQuery(id+"F5.wireOp",EDGE,"E4.sketch_text.stroke-7"),sQuery(id+"F5.wireOp",EDGE,"E4.sketch_text.stroke-8"),sQuery(id+"F5.wireOp",EDGE,"E4.sketch_text.stroke-9"),sQuery(id+"F5.wireOp",EDGE,"E4.sketch_text.stroke-10"),sQuery(id+"F5.wireOp",EDGE,"E4.sketch_text.stroke-11"),sQuery(id+"F5.wireOp",EDGE,"E4.sketch_text.stroke-12"),sQuery(id+"F5.wireOp",EDGE,"E4.sketch_text.stroke-13"),sQuery(id+"F5.wireOp",EDGE,"E4.sketch_text.stroke-14"),sQuery(id+"F5.wireOp",EDGE,"E4.sketch_text.stroke-15"),sQuery(id+"F5.wireOp",EDGE,"E4.sketch_text.stroke-16"),sQuery(id+"F5.wireOp",EDGE,"E4.sketch_text.stroke-17"),sQuery(id+"F5.wireOp",EDGE,"E4.sketch_text.stroke-18"),sQuery(id+"F5.wireOp",EDGE,"E4.sketch_text.stroke-19")])]});
            var Q7;
            Q7=makeQuery(id+"F6.opExtrude","SWEPT_BODY",BODY,{"disambiguationData":[OSD([sQuery(id+"F5.wireOp",EDGE,"E4.sketch_text.stroke-20"),sQuery(id+"F5.wireOp",EDGE,"E4.sketch_text.stroke-21"),sQuery(id+"F5.wireOp",EDGE,"E4.sketch_text.stroke-22"),sQuery(id+"F5.wireOp",EDGE,"E4.sketch_text.stroke-23")])]});
            var Q8;
            Q8=makeQuery(id+"F6.opExtrude","SWEPT_BODY",BODY,{"disambiguationData":[OSD([sQuery(id+"F5.wireOp",EDGE,"E4.sketch_text.stroke-24"),sQuery(id+"F5.wireOp",EDGE,"E4.sketch_text.stroke-25"),sQuery(id+"F5.wireOp",EDGE,"E4.sketch_text.stroke-26"),sQuery(id+"F5.wireOp",EDGE,"E4.sketch_text.stroke-27")])]});
            var Q9;
            Q9=makeQuery(id+"F6.opExtrude","SWEPT_BODY",BODY,{"disambiguationData":[OSD([sQuery(id+"F5.wireOp",EDGE,"E4.sketch_text.stroke-28"),sQuery(id+"F5.wireOp",EDGE,"E4.sketch_text.stroke-29"),sQuery(id+"F5.wireOp",EDGE,"E4.sketch_text.stroke-30"),sQuery(id+"F5.wireOp",EDGE,"E4.sketch_text.stroke-31")])]});
            var Q10;
            Q10=makeQuery(id+"F6.opExtrude","SWEPT_BODY",BODY,{"disambiguationData":[OSD([sQuery(id+"F5.wireOp",EDGE,"E4.sketch_text.stroke-32"),sQuery(id+"F5.wireOp",EDGE,"E4.sketch_text.stroke-33"),sQuery(id+"F5.wireOp",EDGE,"E4.sketch_text.stroke-34"),sQuery(id+"F5.wireOp",EDGE,"E4.sketch_text.stroke-35")])]});
            var Q11;
            Q11=makeQuery(id+"F6.opExtrude","SWEPT_BODY",BODY,{"disambiguationData":[OSD([sQuery(id+"F5.wireOp",EDGE,"E4.sketch_text.stroke-36"),sQuery(id+"F5.wireOp",EDGE,"E4.sketch_text.stroke-37"),sQuery(id+"F5.wireOp",EDGE,"E4.sketch_text.stroke-38"),sQuery(id+"F5.wireOp",EDGE,"E4.sketch_text.stroke-39"),sQuery(id+"F5.wireOp",EDGE,"E4.sketch_text.stroke-40"),sQuery(id+"F5.wireOp",EDGE,"E4.sketch_text.stroke-41"),sQuery(id+"F5.wireOp",EDGE,"E4.sketch_text.stroke-42"),sQuery(id+"F5.wireOp",EDGE,"E4.sketch_text.stroke-43"),sQuery(id+"F5.wireOp",EDGE,"E4.sketch_text.stroke-44"),sQuery(id+"F5.wireOp",EDGE,"E4.sketch_text.stroke-45"),sQuery(id+"F5.wireOp",EDGE,"E4.sketch_text.stroke-46"),sQuery(id+"F5.wireOp",EDGE,"E4.sketch_text.stroke-47"),sQuery(id+"F5.wireOp",EDGE,"E4.sketch_text.stroke-48"),sQuery(id+"F5.wireOp",EDGE,"E4.sketch_text.stroke-49"),sQuery(id+"F5.wireOp",EDGE,"E4.sketch_text.stroke-50"),sQuery(id+"F5.wireOp",EDGE,"E4.sketch_text.stroke-51"),sQuery(id+"F5.wireOp",EDGE,"E4.sketch_text.stroke-52"),sQuery(id+"F5.wireOp",EDGE,"E4.sketch_text.stroke-53"),sQuery(id+"F5.wireOp",EDGE,"E4.sketch_text.stroke-54"),sQuery(id+"F5.wireOp",EDGE,"E4.sketch_text.stroke-55"),sQuery(id+"F5.wireOp",EDGE,"E4.sketch_text.stroke-56"),sQuery(id+"F5.wireOp",EDGE,"E4.sketch_text.stroke-57"),sQuery(id+"F5.wireOp",EDGE,"E4.sketch_text.stroke-58"),sQuery(id+"F5.wireOp",EDGE,"E4.sketch_text.stroke-59"),sQuery(id+"F5.wireOp",EDGE,"E4.sketch_text.stroke-60"),sQuery(id+"F5.wireOp",EDGE,"E4.sketch_text.stroke-61"),sQuery(id+"F5.wireOp",EDGE,"E4.sketch_text.stroke-62"),sQuery(id+"F5.wireOp",EDGE,"E4.sketch_text.stroke-63"),sQuery(id+"F5.wireOp",EDGE,"E4.sketch_text.stroke-64"),sQuery(id+"F5.wireOp",EDGE,"E4.sketch_text.stroke-65"),sQuery(id+"F5.wireOp",EDGE,"E4.sketch_text.stroke-66"),sQuery(id+"F5.wireOp",EDGE,"E4.sketch_text.stroke-67")])]});
            booleanBodies(context, id + "F12", {"operationType" : BooleanOperationType.SUBTRACTION, "tools" : qUnion([Q0, Q1, Q2, Q3, Q4, Q5]), "targets" : qUnion([Q6, Q7, Q8, Q9, Q10, Q11])});
        }
        {
            var Q0;
            Q0=makeQuery(id+"F6.opExtrude","SWEPT_BODY",BODY,{"disambiguationData":[OSD([sQuery(id+"F5.wireOp",EDGE,"E5.sketch_text.stroke-0"),sQuery(id+"F5.wireOp",EDGE,"E5.sketch_text.stroke-1"),sQuery(id+"F5.wireOp",EDGE,"E5.sketch_text.stroke-2"),sQuery(id+"F5.wireOp",EDGE,"E5.sketch_text.stroke-3"),sQuery(id+"F5.wireOp",EDGE,"E5.sketch_text.stroke-4"),sQuery(id+"F5.wireOp",EDGE,"E5.sketch_text.stroke-5"),sQuery(id+"F5.wireOp",EDGE,"E5.sketch_text.stroke-6"),sQuery(id+"F5.wireOp",EDGE,"E5.sketch_text.stroke-7"),sQuery(id+"F5.wireOp",EDGE,"E5.sketch_text.stroke-8"),sQuery(id+"F5.wireOp",EDGE,"E5.sketch_text.stroke-9"),sQuery(id+"F5.wireOp",EDGE,"E5.sketch_text.stroke-10"),sQuery(id+"F5.wireOp",EDGE,"E5.sketch_text.stroke-11"),sQuery(id+"F5.wireOp",EDGE,"E5.sketch_text.stroke-12"),sQuery(id+"F5.wireOp",EDGE,"E5.sketch_text.stroke-13"),sQuery(id+"F5.wireOp",EDGE,"E5.sketch_text.stroke-14"),sQuery(id+"F5.wireOp",EDGE,"E5.sketch_text.stroke-15"),sQuery(id+"F5.wireOp",EDGE,"E5.sketch_text.stroke-16"),sQuery(id+"F5.wireOp",EDGE,"E5.sketch_text.stroke-17"),sQuery(id+"F5.wireOp",EDGE,"E5.sketch_text.stroke-18"),sQuery(id+"F5.wireOp",EDGE,"E5.sketch_text.stroke-19"),sQuery(id+"F5.wireOp",EDGE,"E5.sketch_text.stroke-20"),sQuery(id+"F5.wireOp",EDGE,"E5.sketch_text.stroke-21")])]});
            transform(context, id + "F13", {"entities" : qUnion([Q0]), "transformType" : TransformType.TRANSLATION_3D, "dx" : 1 * mm, "dy" : 0 * mm, "dz" : 0 * mm, "makeCopy" : true});
        }
        {
            var Q0;
            Q0=makeQuery(id+"F13.opPattern","COPY",BODY,{"derivedFrom":makeQuery(id+"F6.opExtrude","SWEPT_BODY",BODY,{"disambiguationData":[OSD([sQuery(id+"F5.wireOp",EDGE,"E5.sketch_text.stroke-0"),sQuery(id+"F5.wireOp",EDGE,"E5.sketch_text.stroke-1"),sQuery(id+"F5.wireOp",EDGE,"E5.sketch_text.stroke-2"),sQuery(id+"F5.wireOp",EDGE,"E5.sketch_text.stroke-3"),sQuery(id+"F5.wireOp",EDGE,"E5.sketch_text.stroke-4"),sQuery(id+"F5.wireOp",EDGE,"E5.sketch_text.stroke-5"),sQuery(id+"F5.wireOp",EDGE,"E5.sketch_text.stroke-6"),sQuery(id+"F5.wireOp",EDGE,"E5.sketch_text.stroke-7"),sQuery(id+"F5.wireOp",EDGE,"E5.sketch_text.stroke-8"),sQuery(id+"F5.wireOp",EDGE,"E5.sketch_text.stroke-9"),sQuery(id+"F5.wireOp",EDGE,"E5.sketch_text.stroke-10"),sQuery(id+"F5.wireOp",EDGE,"E5.sketch_text.stroke-11"),sQuery(id+"F5.wireOp",EDGE,"E5.sketch_text.stroke-12"),sQuery(id+"F5.wireOp",EDGE,"E5.sketch_text.stroke-13"),sQuery(id+"F5.wireOp",EDGE,"E5.sketch_text.stroke-14"),sQuery(id+"F5.wireOp",EDGE,"E5.sketch_text.stroke-15"),sQuery(id+"F5.wireOp",EDGE,"E5.sketch_text.stroke-16"),sQuery(id+"F5.wireOp",EDGE,"E5.sketch_text.stroke-17"),sQuery(id+"F5.wireOp",EDGE,"E5.sketch_text.stroke-18"),sQuery(id+"F5.wireOp",EDGE,"E5.sketch_text.stroke-19"),sQuery(id+"F5.wireOp",EDGE,"E5.sketch_text.stroke-20"),sQuery(id+"F5.wireOp",EDGE,"E5.sketch_text.stroke-21")])]}),"instanceName":"1"});
            var Q1;
            Q1=makeQuery(id+"F6.opExtrude","SWEPT_BODY",BODY,{"disambiguationData":[OSD([sQuery(id+"F5.wireOp",EDGE,"E5.sketch_text.stroke-0"),sQuery(id+"F5.wireOp",EDGE,"E5.sketch_text.stroke-1"),sQuery(id+"F5.wireOp",EDGE,"E5.sketch_text.stroke-2"),sQuery(id+"F5.wireOp",EDGE,"E5.sketch_text.stroke-3"),sQuery(id+"F5.wireOp",EDGE,"E5.sketch_text.stroke-4"),sQuery(id+"F5.wireOp",EDGE,"E5.sketch_text.stroke-5"),sQuery(id+"F5.wireOp",EDGE,"E5.sketch_text.stroke-6"),sQuery(id+"F5.wireOp",EDGE,"E5.sketch_text.stroke-7"),sQuery(id+"F5.wireOp",EDGE,"E5.sketch_text.stroke-8"),sQuery(id+"F5.wireOp",EDGE,"E5.sketch_text.stroke-9"),sQuery(id+"F5.wireOp",EDGE,"E5.sketch_text.stroke-10"),sQuery(id+"F5.wireOp",EDGE,"E5.sketch_text.stroke-11"),sQuery(id+"F5.wireOp",EDGE,"E5.sketch_text.stroke-12"),sQuery(id+"F5.wireOp",EDGE,"E5.sketch_text.stroke-13"),sQuery(id+"F5.wireOp",EDGE,"E5.sketch_text.stroke-14"),sQuery(id+"F5.wireOp",EDGE,"E5.sketch_text.stroke-15"),sQuery(id+"F5.wireOp",EDGE,"E5.sketch_text.stroke-16"),sQuery(id+"F5.wireOp",EDGE,"E5.sketch_text.stroke-17"),sQuery(id+"F5.wireOp",EDGE,"E5.sketch_text.stroke-18"),sQuery(id+"F5.wireOp",EDGE,"E5.sketch_text.stroke-19"),sQuery(id+"F5.wireOp",EDGE,"E5.sketch_text.stroke-20"),sQuery(id+"F5.wireOp",EDGE,"E5.sketch_text.stroke-21")])]});
            booleanBodies(context, id + "F14", {"operationType" : BooleanOperationType.SUBTRACTION, "tools" : qUnion([Q0]), "targets" : qUnion([Q1])});
        }
        {
            var Q0;
            Q0=makeQuery(id+"F6.opExtrude","SWEPT_BODY",BODY,{"disambiguationData":[OSD([sQuery(id+"F5.wireOp",EDGE,"E6.sketch_text.stroke-16"),sQuery(id+"F5.wireOp",EDGE,"E6.sketch_text.stroke-17"),sQuery(id+"F5.wireOp",EDGE,"E6.sketch_text.stroke-18"),sQuery(id+"F5.wireOp",EDGE,"E6.sketch_text.stroke-19"),sQuery(id+"F5.wireOp",EDGE,"E6.sketch_text.stroke-20"),sQuery(id+"F5.wireOp",EDGE,"E6.sketch_text.stroke-21"),sQuery(id+"F5.wireOp",EDGE,"E6.sketch_text.stroke-22"),sQuery(id+"F5.wireOp",EDGE,"E6.sketch_text.stroke-23"),sQuery(id+"F5.wireOp",EDGE,"E6.sketch_text.stroke-24"),sQuery(id+"F5.wireOp",EDGE,"E6.sketch_text.stroke-25"),sQuery(id+"F5.wireOp",EDGE,"E6.sketch_text.stroke-26"),sQuery(id+"F5.wireOp",EDGE,"E6.sketch_text.stroke-27"),sQuery(id+"F5.wireOp",EDGE,"E6.sketch_text.stroke-28"),sQuery(id+"F5.wireOp",EDGE,"E6.sketch_text.stroke-29"),sQuery(id+"F5.wireOp",EDGE,"E6.sketch_text.stroke-30"),sQuery(id+"F5.wireOp",EDGE,"E6.sketch_text.stroke-31"),sQuery(id+"F5.wireOp",EDGE,"E6.sketch_text.stroke-32"),sQuery(id+"F5.wireOp",EDGE,"E6.sketch_text.stroke-33"),sQuery(id+"F5.wireOp",EDGE,"E6.sketch_text.stroke-34"),sQuery(id+"F5.wireOp",EDGE,"E6.sketch_text.stroke-35"),sQuery(id+"F5.wireOp",EDGE,"E6.sketch_text.stroke-36"),sQuery(id+"F5.wireOp",EDGE,"E6.sketch_text.stroke-37")])]});
            var Q1;
            Q1=makeQuery(id+"F6.opExtrude","SWEPT_BODY",BODY,{"disambiguationData":[OSD([sQuery(id+"F5.wireOp",EDGE,"E6.sketch_text.stroke-0"),sQuery(id+"F5.wireOp",EDGE,"E6.sketch_text.stroke-1"),sQuery(id+"F5.wireOp",EDGE,"E6.sketch_text.stroke-2"),sQuery(id+"F5.wireOp",EDGE,"E6.sketch_text.stroke-3"),sQuery(id+"F5.wireOp",EDGE,"E6.sketch_text.stroke-4"),sQuery(id+"F5.wireOp",EDGE,"E6.sketch_text.stroke-5"),sQuery(id+"F5.wireOp",EDGE,"E6.sketch_text.stroke-6"),sQuery(id+"F5.wireOp",EDGE,"E6.sketch_text.stroke-7"),sQuery(id+"F5.wireOp",EDGE,"E6.sketch_text.stroke-8"),sQuery(id+"F5.wireOp",EDGE,"E6.sketch_text.stroke-9"),sQuery(id+"F5.wireOp",EDGE,"E6.sketch_text.stroke-10"),sQuery(id+"F5.wireOp",EDGE,"E6.sketch_text.stroke-11"),sQuery(id+"F5.wireOp",EDGE,"E6.sketch_text.stroke-12"),sQuery(id+"F5.wireOp",EDGE,"E6.sketch_text.stroke-13"),sQuery(id+"F5.wireOp",EDGE,"E6.sketch_text.stroke-14"),sQuery(id+"F5.wireOp",EDGE,"E6.sketch_text.stroke-15")])]});
            transform(context, id + "F15", {"entities" : qUnion([Q0, Q1]), "transformType" : TransformType.TRANSLATION_3D, "dx" : 1 * mm, "dy" : 0 * mm, "dz" : 0 * mm, "makeCopy" : true});
        }
        {
            var Q0;
            Q0=makeQuery(id+"F15.opPattern","COPY",BODY,{"derivedFrom":makeQuery(id+"F6.opExtrude","SWEPT_BODY",BODY,{"disambiguationData":[OSD([sQuery(id+"F5.wireOp",EDGE,"E6.sketch_text.stroke-16"),sQuery(id+"F5.wireOp",EDGE,"E6.sketch_text.stroke-17"),sQuery(id+"F5.wireOp",EDGE,"E6.sketch_text.stroke-18"),sQuery(id+"F5.wireOp",EDGE,"E6.sketch_text.stroke-19"),sQuery(id+"F5.wireOp",EDGE,"E6.sketch_text.stroke-20"),sQuery(id+"F5.wireOp",EDGE,"E6.sketch_text.stroke-21"),sQuery(id+"F5.wireOp",EDGE,"E6.sketch_text.stroke-22"),sQuery(id+"F5.wireOp",EDGE,"E6.sketch_text.stroke-23"),sQuery(id+"F5.wireOp",EDGE,"E6.sketch_text.stroke-24"),sQuery(id+"F5.wireOp",EDGE,"E6.sketch_text.stroke-25"),sQuery(id+"F5.wireOp",EDGE,"E6.sketch_text.stroke-26"),sQuery(id+"F5.wireOp",EDGE,"E6.sketch_text.stroke-27"),sQuery(id+"F5.wireOp",EDGE,"E6.sketch_text.stroke-28"),sQuery(id+"F5.wireOp",EDGE,"E6.sketch_text.stroke-29"),sQuery(id+"F5.wireOp",EDGE,"E6.sketch_text.stroke-30"),sQuery(id+"F5.wireOp",EDGE,"E6.sketch_text.stroke-31"),sQuery(id+"F5.wireOp",EDGE,"E6.sketch_text.stroke-32"),sQuery(id+"F5.wireOp",EDGE,"E6.sketch_text.stroke-33"),sQuery(id+"F5.wireOp",EDGE,"E6.sketch_text.stroke-34"),sQuery(id+"F5.wireOp",EDGE,"E6.sketch_text.stroke-35"),sQuery(id+"F5.wireOp",EDGE,"E6.sketch_text.stroke-36"),sQuery(id+"F5.wireOp",EDGE,"E6.sketch_text.stroke-37")])]}),"instanceName":"1"});
            var Q1;
            Q1=makeQuery(id+"F15.opPattern","COPY",BODY,{"derivedFrom":makeQuery(id+"F6.opExtrude","SWEPT_BODY",BODY,{"disambiguationData":[OSD([sQuery(id+"F5.wireOp",EDGE,"E6.sketch_text.stroke-0"),sQuery(id+"F5.wireOp",EDGE,"E6.sketch_text.stroke-1"),sQuery(id+"F5.wireOp",EDGE,"E6.sketch_text.stroke-2"),sQuery(id+"F5.wireOp",EDGE,"E6.sketch_text.stroke-3"),sQuery(id+"F5.wireOp",EDGE,"E6.sketch_text.stroke-4"),sQuery(id+"F5.wireOp",EDGE,"E6.sketch_text.stroke-5"),sQuery(id+"F5.wireOp",EDGE,"E6.sketch_text.stroke-6"),sQuery(id+"F5.wireOp",EDGE,"E6.sketch_text.stroke-7"),sQuery(id+"F5.wireOp",EDGE,"E6.sketch_text.stroke-8"),sQuery(id+"F5.wireOp",EDGE,"E6.sketch_text.stroke-9"),sQuery(id+"F5.wireOp",EDGE,"E6.sketch_text.stroke-10"),sQuery(id+"F5.wireOp",EDGE,"E6.sketch_text.stroke-11"),sQuery(id+"F5.wireOp",EDGE,"E6.sketch_text.stroke-12"),sQuery(id+"F5.wireOp",EDGE,"E6.sketch_text.stroke-13"),sQuery(id+"F5.wireOp",EDGE,"E6.sketch_text.stroke-14"),sQuery(id+"F5.wireOp",EDGE,"E6.sketch_text.stroke-15")])]}),"instanceName":"1"});
            var Q2;
            Q2=makeQuery(id+"F6.opExtrude","SWEPT_BODY",BODY,{"disambiguationData":[OSD([sQuery(id+"F5.wireOp",EDGE,"E6.sketch_text.stroke-16"),sQuery(id+"F5.wireOp",EDGE,"E6.sketch_text.stroke-17"),sQuery(id+"F5.wireOp",EDGE,"E6.sketch_text.stroke-18"),sQuery(id+"F5.wireOp",EDGE,"E6.sketch_text.stroke-19"),sQuery(id+"F5.wireOp",EDGE,"E6.sketch_text.stroke-20"),sQuery(id+"F5.wireOp",EDGE,"E6.sketch_text.stroke-21"),sQuery(id+"F5.wireOp",EDGE,"E6.sketch_text.stroke-22"),sQuery(id+"F5.wireOp",EDGE,"E6.sketch_text.stroke-23"),sQuery(id+"F5.wireOp",EDGE,"E6.sketch_text.stroke-24"),sQuery(id+"F5.wireOp",EDGE,"E6.sketch_text.stroke-25"),sQuery(id+"F5.wireOp",EDGE,"E6.sketch_text.stroke-26"),sQuery(id+"F5.wireOp",EDGE,"E6.sketch_text.stroke-27"),sQuery(id+"F5.wireOp",EDGE,"E6.sketch_text.stroke-28"),sQuery(id+"F5.wireOp",EDGE,"E6.sketch_text.stroke-29"),sQuery(id+"F5.wireOp",EDGE,"E6.sketch_text.stroke-30"),sQuery(id+"F5.wireOp",EDGE,"E6.sketch_text.stroke-31"),sQuery(id+"F5.wireOp",EDGE,"E6.sketch_text.stroke-32"),sQuery(id+"F5.wireOp",EDGE,"E6.sketch_text.stroke-33"),sQuery(id+"F5.wireOp",EDGE,"E6.sketch_text.stroke-34"),sQuery(id+"F5.wireOp",EDGE,"E6.sketch_text.stroke-35"),sQuery(id+"F5.wireOp",EDGE,"E6.sketch_text.stroke-36"),sQuery(id+"F5.wireOp",EDGE,"E6.sketch_text.stroke-37")])]});
            var Q3;
            Q3=makeQuery(id+"F6.opExtrude","SWEPT_BODY",BODY,{"disambiguationData":[OSD([sQuery(id+"F5.wireOp",EDGE,"E6.sketch_text.stroke-0"),sQuery(id+"F5.wireOp",EDGE,"E6.sketch_text.stroke-1"),sQuery(id+"F5.wireOp",EDGE,"E6.sketch_text.stroke-2"),sQuery(id+"F5.wireOp",EDGE,"E6.sketch_text.stroke-3"),sQuery(id+"F5.wireOp",EDGE,"E6.sketch_text.stroke-4"),sQuery(id+"F5.wireOp",EDGE,"E6.sketch_text.stroke-5"),sQuery(id+"F5.wireOp",EDGE,"E6.sketch_text.stroke-6"),sQuery(id+"F5.wireOp",EDGE,"E6.sketch_text.stroke-7"),sQuery(id+"F5.wireOp",EDGE,"E6.sketch_text.stroke-8"),sQuery(id+"F5.wireOp",EDGE,"E6.sketch_text.stroke-9"),sQuery(id+"F5.wireOp",EDGE,"E6.sketch_text.stroke-10"),sQuery(id+"F5.wireOp",EDGE,"E6.sketch_text.stroke-11"),sQuery(id+"F5.wireOp",EDGE,"E6.sketch_text.stroke-12"),sQuery(id+"F5.wireOp",EDGE,"E6.sketch_text.stroke-13"),sQuery(id+"F5.wireOp",EDGE,"E6.sketch_text.stroke-14"),sQuery(id+"F5.wireOp",EDGE,"E6.sketch_text.stroke-15")])]});
            booleanBodies(context, id + "F16", {"operationType" : BooleanOperationType.SUBTRACTION, "tools" : qUnion([Q0, Q1]), "targets" : qUnion([Q2, Q3])});
        }
        {
            var Q0;
            Q0=makeQuery(id+"F6.opExtrude","SWEPT_BODY",BODY,{"disambiguationData":[OSD([sQuery(id+"F5.wireOp",EDGE,"E6.sketch_text.stroke-16"),sQuery(id+"F5.wireOp",EDGE,"E6.sketch_text.stroke-17"),sQuery(id+"F5.wireOp",EDGE,"E6.sketch_text.stroke-18"),sQuery(id+"F5.wireOp",EDGE,"E6.sketch_text.stroke-19"),sQuery(id+"F5.wireOp",EDGE,"E6.sketch_text.stroke-20"),sQuery(id+"F5.wireOp",EDGE,"E6.sketch_text.stroke-21"),sQuery(id+"F5.wireOp",EDGE,"E6.sketch_text.stroke-22"),sQuery(id+"F5.wireOp",EDGE,"E6.sketch_text.stroke-23"),sQuery(id+"F5.wireOp",EDGE,"E6.sketch_text.stroke-24"),sQuery(id+"F5.wireOp",EDGE,"E6.sketch_text.stroke-25"),sQuery(id+"F5.wireOp",EDGE,"E6.sketch_text.stroke-26"),sQuery(id+"F5.wireOp",EDGE,"E6.sketch_text.stroke-27"),sQuery(id+"F5.wireOp",EDGE,"E6.sketch_text.stroke-28"),sQuery(id+"F5.wireOp",EDGE,"E6.sketch_text.stroke-29"),sQuery(id+"F5.wireOp",EDGE,"E6.sketch_text.stroke-30"),sQuery(id+"F5.wireOp",EDGE,"E6.sketch_text.stroke-31"),sQuery(id+"F5.wireOp",EDGE,"E6.sketch_text.stroke-32"),sQuery(id+"F5.wireOp",EDGE,"E6.sketch_text.stroke-33"),sQuery(id+"F5.wireOp",EDGE,"E6.sketch_text.stroke-34"),sQuery(id+"F5.wireOp",EDGE,"E6.sketch_text.stroke-35"),sQuery(id+"F5.wireOp",EDGE,"E6.sketch_text.stroke-36"),sQuery(id+"F5.wireOp",EDGE,"E6.sketch_text.stroke-37")])]});
            var Q1;
            Q1=makeQuery(id+"F6.opExtrude","SWEPT_BODY",BODY,{"disambiguationData":[OSD([sQuery(id+"F5.wireOp",EDGE,"E6.sketch_text.stroke-0"),sQuery(id+"F5.wireOp",EDGE,"E6.sketch_text.stroke-1"),sQuery(id+"F5.wireOp",EDGE,"E6.sketch_text.stroke-2"),sQuery(id+"F5.wireOp",EDGE,"E6.sketch_text.stroke-3"),sQuery(id+"F5.wireOp",EDGE,"E6.sketch_text.stroke-4"),sQuery(id+"F5.wireOp",EDGE,"E6.sketch_text.stroke-5"),sQuery(id+"F5.wireOp",EDGE,"E6.sketch_text.stroke-6"),sQuery(id+"F5.wireOp",EDGE,"E6.sketch_text.stroke-7"),sQuery(id+"F5.wireOp",EDGE,"E6.sketch_text.stroke-8"),sQuery(id+"F5.wireOp",EDGE,"E6.sketch_text.stroke-9"),sQuery(id+"F5.wireOp",EDGE,"E6.sketch_text.stroke-10"),sQuery(id+"F5.wireOp",EDGE,"E6.sketch_text.stroke-11"),sQuery(id+"F5.wireOp",EDGE,"E6.sketch_text.stroke-12"),sQuery(id+"F5.wireOp",EDGE,"E6.sketch_text.stroke-13"),sQuery(id+"F5.wireOp",EDGE,"E6.sketch_text.stroke-14"),sQuery(id+"F5.wireOp",EDGE,"E6.sketch_text.stroke-15")])]});
            var Q2;
            Q2=makeQuery(id+"F6.opExtrude","SWEPT_BODY",BODY,{"disambiguationData":[OSD([sQuery(id+"F5.wireOp",EDGE,"E5.sketch_text.stroke-0"),sQuery(id+"F5.wireOp",EDGE,"E5.sketch_text.stroke-1"),sQuery(id+"F5.wireOp",EDGE,"E5.sketch_text.stroke-2"),sQuery(id+"F5.wireOp",EDGE,"E5.sketch_text.stroke-3"),sQuery(id+"F5.wireOp",EDGE,"E5.sketch_text.stroke-4"),sQuery(id+"F5.wireOp",EDGE,"E5.sketch_text.stroke-5"),sQuery(id+"F5.wireOp",EDGE,"E5.sketch_text.stroke-6"),sQuery(id+"F5.wireOp",EDGE,"E5.sketch_text.stroke-7"),sQuery(id+"F5.wireOp",EDGE,"E5.sketch_text.stroke-8"),sQuery(id+"F5.wireOp",EDGE,"E5.sketch_text.stroke-9"),sQuery(id+"F5.wireOp",EDGE,"E5.sketch_text.stroke-10"),sQuery(id+"F5.wireOp",EDGE,"E5.sketch_text.stroke-11"),sQuery(id+"F5.wireOp",EDGE,"E5.sketch_text.stroke-12"),sQuery(id+"F5.wireOp",EDGE,"E5.sketch_text.stroke-13"),sQuery(id+"F5.wireOp",EDGE,"E5.sketch_text.stroke-14"),sQuery(id+"F5.wireOp",EDGE,"E5.sketch_text.stroke-15"),sQuery(id+"F5.wireOp",EDGE,"E5.sketch_text.stroke-16"),sQuery(id+"F5.wireOp",EDGE,"E5.sketch_text.stroke-17"),sQuery(id+"F5.wireOp",EDGE,"E5.sketch_text.stroke-18"),sQuery(id+"F5.wireOp",EDGE,"E5.sketch_text.stroke-19"),sQuery(id+"F5.wireOp",EDGE,"E5.sketch_text.stroke-20"),sQuery(id+"F5.wireOp",EDGE,"E5.sketch_text.stroke-21")])]});
            var Q3;
            Q3=makeQuery(id+"F6.opExtrude","SWEPT_BODY",BODY,{"disambiguationData":[OSD([sQuery(id+"F5.wireOp",EDGE,"E4.sketch_text.stroke-36"),sQuery(id+"F5.wireOp",EDGE,"E4.sketch_text.stroke-37"),sQuery(id+"F5.wireOp",EDGE,"E4.sketch_text.stroke-38"),sQuery(id+"F5.wireOp",EDGE,"E4.sketch_text.stroke-39"),sQuery(id+"F5.wireOp",EDGE,"E4.sketch_text.stroke-40"),sQuery(id+"F5.wireOp",EDGE,"E4.sketch_text.stroke-41"),sQuery(id+"F5.wireOp",EDGE,"E4.sketch_text.stroke-42"),sQuery(id+"F5.wireOp",EDGE,"E4.sketch_text.stroke-43"),sQuery(id+"F5.wireOp",EDGE,"E4.sketch_text.stroke-44"),sQuery(id+"F5.wireOp",EDGE,"E4.sketch_text.stroke-45"),sQuery(id+"F5.wireOp",EDGE,"E4.sketch_text.stroke-46"),sQuery(id+"F5.wireOp",EDGE,"E4.sketch_text.stroke-47"),sQuery(id+"F5.wireOp",EDGE,"E4.sketch_text.stroke-48"),sQuery(id+"F5.wireOp",EDGE,"E4.sketch_text.stroke-49"),sQuery(id+"F5.wireOp",EDGE,"E4.sketch_text.stroke-50"),sQuery(id+"F5.wireOp",EDGE,"E4.sketch_text.stroke-51"),sQuery(id+"F5.wireOp",EDGE,"E4.sketch_text.stroke-52"),sQuery(id+"F5.wireOp",EDGE,"E4.sketch_text.stroke-53"),sQuery(id+"F5.wireOp",EDGE,"E4.sketch_text.stroke-54"),sQuery(id+"F5.wireOp",EDGE,"E4.sketch_text.stroke-55"),sQuery(id+"F5.wireOp",EDGE,"E4.sketch_text.stroke-56"),sQuery(id+"F5.wireOp",EDGE,"E4.sketch_text.stroke-57"),sQuery(id+"F5.wireOp",EDGE,"E4.sketch_text.stroke-58"),sQuery(id+"F5.wireOp",EDGE,"E4.sketch_text.stroke-59"),sQuery(id+"F5.wireOp",EDGE,"E4.sketch_text.stroke-60"),sQuery(id+"F5.wireOp",EDGE,"E4.sketch_text.stroke-61"),sQuery(id+"F5.wireOp",EDGE,"E4.sketch_text.stroke-62"),sQuery(id+"F5.wireOp",EDGE,"E4.sketch_text.stroke-63"),sQuery(id+"F5.wireOp",EDGE,"E4.sketch_text.stroke-64"),sQuery(id+"F5.wireOp",EDGE,"E4.sketch_text.stroke-65"),sQuery(id+"F5.wireOp",EDGE,"E4.sketch_text.stroke-66"),sQuery(id+"F5.wireOp",EDGE,"E4.sketch_text.stroke-67")])]});
            var Q4;
            Q4=makeQuery(id+"F6.opExtrude","SWEPT_BODY",BODY,{"disambiguationData":[OSD([sQuery(id+"F5.wireOp",EDGE,"E4.sketch_text.stroke-32"),sQuery(id+"F5.wireOp",EDGE,"E4.sketch_text.stroke-33"),sQuery(id+"F5.wireOp",EDGE,"E4.sketch_text.stroke-34"),sQuery(id+"F5.wireOp",EDGE,"E4.sketch_text.stroke-35")])]});
            var Q5;
            Q5=makeQuery(id+"F6.opExtrude","SWEPT_BODY",BODY,{"disambiguationData":[OSD([sQuery(id+"F5.wireOp",EDGE,"E4.sketch_text.stroke-28"),sQuery(id+"F5.wireOp",EDGE,"E4.sketch_text.stroke-29"),sQuery(id+"F5.wireOp",EDGE,"E4.sketch_text.stroke-30"),sQuery(id+"F5.wireOp",EDGE,"E4.sketch_text.stroke-31")])]});
            var Q6;
            Q6=makeQuery(id+"F6.opExtrude","SWEPT_BODY",BODY,{"disambiguationData":[OSD([sQuery(id+"F5.wireOp",EDGE,"E4.sketch_text.stroke-20"),sQuery(id+"F5.wireOp",EDGE,"E4.sketch_text.stroke-21"),sQuery(id+"F5.wireOp",EDGE,"E4.sketch_text.stroke-22"),sQuery(id+"F5.wireOp",EDGE,"E4.sketch_text.stroke-23")])]});
            var Q7;
            Q7=makeQuery(id+"F6.opExtrude","SWEPT_BODY",BODY,{"disambiguationData":[OSD([sQuery(id+"F5.wireOp",EDGE,"E4.sketch_text.stroke-24"),sQuery(id+"F5.wireOp",EDGE,"E4.sketch_text.stroke-25"),sQuery(id+"F5.wireOp",EDGE,"E4.sketch_text.stroke-26"),sQuery(id+"F5.wireOp",EDGE,"E4.sketch_text.stroke-27")])]});
            var Q8;
            Q8=makeQuery(id+"F6.opExtrude","SWEPT_BODY",BODY,{"disambiguationData":[OSD([sQuery(id+"F5.wireOp",EDGE,"E4.sketch_text.stroke-0"),sQuery(id+"F5.wireOp",EDGE,"E4.sketch_text.stroke-1"),sQuery(id+"F5.wireOp",EDGE,"E4.sketch_text.stroke-2"),sQuery(id+"F5.wireOp",EDGE,"E4.sketch_text.stroke-3"),sQuery(id+"F5.wireOp",EDGE,"E4.sketch_text.stroke-4"),sQuery(id+"F5.wireOp",EDGE,"E4.sketch_text.stroke-5"),sQuery(id+"F5.wireOp",EDGE,"E4.sketch_text.stroke-6"),sQuery(id+"F5.wireOp",EDGE,"E4.sketch_text.stroke-7"),sQuery(id+"F5.wireOp",EDGE,"E4.sketch_text.stroke-8"),sQuery(id+"F5.wireOp",EDGE,"E4.sketch_text.stroke-9"),sQuery(id+"F5.wireOp",EDGE,"E4.sketch_text.stroke-10"),sQuery(id+"F5.wireOp",EDGE,"E4.sketch_text.stroke-11"),sQuery(id+"F5.wireOp",EDGE,"E4.sketch_text.stroke-12"),sQuery(id+"F5.wireOp",EDGE,"E4.sketch_text.stroke-13"),sQuery(id+"F5.wireOp",EDGE,"E4.sketch_text.stroke-14"),sQuery(id+"F5.wireOp",EDGE,"E4.sketch_text.stroke-15"),sQuery(id+"F5.wireOp",EDGE,"E4.sketch_text.stroke-16"),sQuery(id+"F5.wireOp",EDGE,"E4.sketch_text.stroke-17"),sQuery(id+"F5.wireOp",EDGE,"E4.sketch_text.stroke-18"),sQuery(id+"F5.wireOp",EDGE,"E4.sketch_text.stroke-19")])]});
            var Q9;
            Q9=makeQuery(id+"F6.opExtrude","SWEPT_BODY",BODY,{"disambiguationData":[OSD([sQuery(id+"F5.wireOp",EDGE,"E3.sketch_text.stroke-52"),sQuery(id+"F5.wireOp",EDGE,"E3.sketch_text.stroke-53"),sQuery(id+"F5.wireOp",EDGE,"E3.sketch_text.stroke-54"),sQuery(id+"F5.wireOp",EDGE,"E3.sketch_text.stroke-55")])]});
            var Q10;
            Q10=makeQuery(id+"F6.opExtrude","SWEPT_BODY",BODY,{"disambiguationData":[OSD([sQuery(id+"F5.wireOp",EDGE,"E3.sketch_text.stroke-44"),sQuery(id+"F5.wireOp",EDGE,"E3.sketch_text.stroke-45"),sQuery(id+"F5.wireOp",EDGE,"E3.sketch_text.stroke-46"),sQuery(id+"F5.wireOp",EDGE,"E3.sketch_text.stroke-47"),sQuery(id+"F5.wireOp",EDGE,"E3.sketch_text.stroke-48"),sQuery(id+"F5.wireOp",EDGE,"E3.sketch_text.stroke-49"),sQuery(id+"F5.wireOp",EDGE,"E3.sketch_text.stroke-50"),sQuery(id+"F5.wireOp",EDGE,"E3.sketch_text.stroke-51")])]});
            var Q11;
            Q11=makeQuery(id+"F6.opExtrude","SWEPT_BODY",BODY,{"disambiguationData":[OSD([sQuery(id+"F5.wireOp",EDGE,"E3.sketch_text.stroke-4"),sQuery(id+"F5.wireOp",EDGE,"E3.sketch_text.stroke-5"),sQuery(id+"F5.wireOp",EDGE,"E3.sketch_text.stroke-6"),sQuery(id+"F5.wireOp",EDGE,"E3.sketch_text.stroke-7"),sQuery(id+"F5.wireOp",EDGE,"E3.sketch_text.stroke-8"),sQuery(id+"F5.wireOp",EDGE,"E3.sketch_text.stroke-9"),sQuery(id+"F5.wireOp",EDGE,"E3.sketch_text.stroke-10"),sQuery(id+"F5.wireOp",EDGE,"E3.sketch_text.stroke-11"),sQuery(id+"F5.wireOp",EDGE,"E3.sketch_text.stroke-12"),sQuery(id+"F5.wireOp",EDGE,"E3.sketch_text.stroke-13"),sQuery(id+"F5.wireOp",EDGE,"E3.sketch_text.stroke-14"),sQuery(id+"F5.wireOp",EDGE,"E3.sketch_text.stroke-15"),sQuery(id+"F5.wireOp",EDGE,"E3.sketch_text.stroke-16"),sQuery(id+"F5.wireOp",EDGE,"E3.sketch_text.stroke-17"),sQuery(id+"F5.wireOp",EDGE,"E3.sketch_text.stroke-18"),sQuery(id+"F5.wireOp",EDGE,"E3.sketch_text.stroke-19"),sQuery(id+"F5.wireOp",EDGE,"E3.sketch_text.stroke-20"),sQuery(id+"F5.wireOp",EDGE,"E3.sketch_text.stroke-21"),sQuery(id+"F5.wireOp",EDGE,"E3.sketch_text.stroke-22"),sQuery(id+"F5.wireOp",EDGE,"E3.sketch_text.stroke-23"),sQuery(id+"F5.wireOp",EDGE,"E3.sketch_text.stroke-24"),sQuery(id+"F5.wireOp",EDGE,"E3.sketch_text.stroke-25"),sQuery(id+"F5.wireOp",EDGE,"E3.sketch_text.stroke-26"),sQuery(id+"F5.wireOp",EDGE,"E3.sketch_text.stroke-27"),sQuery(id+"F5.wireOp",EDGE,"E3.sketch_text.stroke-28"),sQuery(id+"F5.wireOp",EDGE,"E3.sketch_text.stroke-29"),sQuery(id+"F5.wireOp",EDGE,"E3.sketch_text.stroke-30"),sQuery(id+"F5.wireOp",EDGE,"E3.sketch_text.stroke-31"),sQuery(id+"F5.wireOp",EDGE,"E3.sketch_text.stroke-32"),sQuery(id+"F5.wireOp",EDGE,"E3.sketch_text.stroke-33"),sQuery(id+"F5.wireOp",EDGE,"E3.sketch_text.stroke-34"),sQuery(id+"F5.wireOp",EDGE,"E3.sketch_text.stroke-35"),sQuery(id+"F5.wireOp",EDGE,"E3.sketch_text.stroke-36"),sQuery(id+"F5.wireOp",EDGE,"E3.sketch_text.stroke-37"),sQuery(id+"F5.wireOp",EDGE,"E3.sketch_text.stroke-38"),sQuery(id+"F5.wireOp",EDGE,"E3.sketch_text.stroke-39"),sQuery(id+"F5.wireOp",EDGE,"E3.sketch_text.stroke-40"),sQuery(id+"F5.wireOp",EDGE,"E3.sketch_text.stroke-41"),sQuery(id+"F5.wireOp",EDGE,"E3.sketch_text.stroke-42"),sQuery(id+"F5.wireOp",EDGE,"E3.sketch_text.stroke-43")])]});
            var Q12;
            Q12=makeQuery(id+"F6.opExtrude","SWEPT_BODY",BODY,{"disambiguationData":[OSD([sQuery(id+"F5.wireOp",EDGE,"E2.sketch_text.stroke-0"),sQuery(id+"F5.wireOp",EDGE,"E2.sketch_text.stroke-1"),sQuery(id+"F5.wireOp",EDGE,"E2.sketch_text.stroke-2"),sQuery(id+"F5.wireOp",EDGE,"E2.sketch_text.stroke-3")])]});
            var Q13;
            Q13=makeQuery(id+"F6.opExtrude","SWEPT_BODY",BODY,{"disambiguationData":[OSD([sQuery(id+"F5.wireOp",EDGE,"E2.sketch_text.stroke-4"),sQuery(id+"F5.wireOp",EDGE,"E2.sketch_text.stroke-5"),sQuery(id+"F5.wireOp",EDGE,"E2.sketch_text.stroke-6"),sQuery(id+"F5.wireOp",EDGE,"E2.sketch_text.stroke-7"),sQuery(id+"F5.wireOp",EDGE,"E2.sketch_text.stroke-8"),sQuery(id+"F5.wireOp",EDGE,"E2.sketch_text.stroke-9"),sQuery(id+"F5.wireOp",EDGE,"E2.sketch_text.stroke-10"),sQuery(id+"F5.wireOp",EDGE,"E2.sketch_text.stroke-11"),sQuery(id+"F5.wireOp",EDGE,"E2.sketch_text.stroke-12"),sQuery(id+"F5.wireOp",EDGE,"E2.sketch_text.stroke-13"),sQuery(id+"F5.wireOp",EDGE,"E2.sketch_text.stroke-14"),sQuery(id+"F5.wireOp",EDGE,"E2.sketch_text.stroke-15"),sQuery(id+"F5.wireOp",EDGE,"E2.sketch_text.stroke-16"),sQuery(id+"F5.wireOp",EDGE,"E2.sketch_text.stroke-17"),sQuery(id+"F5.wireOp",EDGE,"E2.sketch_text.stroke-18")])]});
            var Q14;
            Q14=makeQuery(id+"F6.opExtrude","SWEPT_BODY",BODY,{"disambiguationData":[OSD([sQuery(id+"F5.wireOp",EDGE,"E2.sketch_text.stroke-19"),sQuery(id+"F5.wireOp",EDGE,"E2.sketch_text.stroke-20"),sQuery(id+"F5.wireOp",EDGE,"E2.sketch_text.stroke-21"),sQuery(id+"F5.wireOp",EDGE,"E2.sketch_text.stroke-22"),sQuery(id+"F5.wireOp",EDGE,"E2.sketch_text.stroke-23"),sQuery(id+"F5.wireOp",EDGE,"E2.sketch_text.stroke-24"),sQuery(id+"F5.wireOp",EDGE,"E2.sketch_text.stroke-25"),sQuery(id+"F5.wireOp",EDGE,"E2.sketch_text.stroke-26"),sQuery(id+"F5.wireOp",EDGE,"E2.sketch_text.stroke-27"),sQuery(id+"F5.wireOp",EDGE,"E2.sketch_text.stroke-28"),sQuery(id+"F5.wireOp",EDGE,"E2.sketch_text.stroke-29"),sQuery(id+"F5.wireOp",EDGE,"E2.sketch_text.stroke-30"),sQuery(id+"F5.wireOp",EDGE,"E2.sketch_text.stroke-31"),sQuery(id+"F5.wireOp",EDGE,"E2.sketch_text.stroke-32"),sQuery(id+"F5.wireOp",EDGE,"E2.sketch_text.stroke-33")])]});
            var Q15;
            Q15=makeQuery(id+"F6.opExtrude","SWEPT_BODY",BODY,{"disambiguationData":[OSD([sQuery(id+"F5.wireOp",EDGE,"E3.sketch_text.stroke-0"),sQuery(id+"F5.wireOp",EDGE,"E3.sketch_text.stroke-1"),sQuery(id+"F5.wireOp",EDGE,"E3.sketch_text.stroke-2"),sQuery(id+"F5.wireOp",EDGE,"E3.sketch_text.stroke-3")])]});
            transform(context, id + "F17", {"entities" : qUnion([Q0, Q1, Q2, Q3, Q4, Q5, Q6, Q7, Q8, Q9, Q10, Q11, Q12, Q13, Q14, Q15]), "transformType" : TransformType.TRANSLATION_3D, "dx" : -0.5 * mm, "dy" : 0 * mm, "dz" : 0 * mm, "makeCopy" : false});
        }
        {
            var Q0;
            Q0=makeQuery(id+"F6.opExtrude","SWEPT_BODY",BODY,{"disambiguationData":[OSD([sQuery(id+"F5.wireOp",EDGE,"E6.sketch_text.stroke-16"),sQuery(id+"F5.wireOp",EDGE,"E6.sketch_text.stroke-17"),sQuery(id+"F5.wireOp",EDGE,"E6.sketch_text.stroke-18"),sQuery(id+"F5.wireOp",EDGE,"E6.sketch_text.stroke-19"),sQuery(id+"F5.wireOp",EDGE,"E6.sketch_text.stroke-20"),sQuery(id+"F5.wireOp",EDGE,"E6.sketch_text.stroke-21"),sQuery(id+"F5.wireOp",EDGE,"E6.sketch_text.stroke-22"),sQuery(id+"F5.wireOp",EDGE,"E6.sketch_text.stroke-23"),sQuery(id+"F5.wireOp",EDGE,"E6.sketch_text.stroke-24"),sQuery(id+"F5.wireOp",EDGE,"E6.sketch_text.stroke-25"),sQuery(id+"F5.wireOp",EDGE,"E6.sketch_text.stroke-26"),sQuery(id+"F5.wireOp",EDGE,"E6.sketch_text.stroke-27"),sQuery(id+"F5.wireOp",EDGE,"E6.sketch_text.stroke-28"),sQuery(id+"F5.wireOp",EDGE,"E6.sketch_text.stroke-29"),sQuery(id+"F5.wireOp",EDGE,"E6.sketch_text.stroke-30"),sQuery(id+"F5.wireOp",EDGE,"E6.sketch_text.stroke-31"),sQuery(id+"F5.wireOp",EDGE,"E6.sketch_text.stroke-32"),sQuery(id+"F5.wireOp",EDGE,"E6.sketch_text.stroke-33"),sQuery(id+"F5.wireOp",EDGE,"E6.sketch_text.stroke-34"),sQuery(id+"F5.wireOp",EDGE,"E6.sketch_text.stroke-35"),sQuery(id+"F5.wireOp",EDGE,"E6.sketch_text.stroke-36"),sQuery(id+"F5.wireOp",EDGE,"E6.sketch_text.stroke-37")])]});
            var Q1;
            Q1=makeQuery(id+"F6.opExtrude","SWEPT_BODY",BODY,{"disambiguationData":[OSD([sQuery(id+"F5.wireOp",EDGE,"E6.sketch_text.stroke-0"),sQuery(id+"F5.wireOp",EDGE,"E6.sketch_text.stroke-1"),sQuery(id+"F5.wireOp",EDGE,"E6.sketch_text.stroke-2"),sQuery(id+"F5.wireOp",EDGE,"E6.sketch_text.stroke-3"),sQuery(id+"F5.wireOp",EDGE,"E6.sketch_text.stroke-4"),sQuery(id+"F5.wireOp",EDGE,"E6.sketch_text.stroke-5"),sQuery(id+"F5.wireOp",EDGE,"E6.sketch_text.stroke-6"),sQuery(id+"F5.wireOp",EDGE,"E6.sketch_text.stroke-7"),sQuery(id+"F5.wireOp",EDGE,"E6.sketch_text.stroke-8"),sQuery(id+"F5.wireOp",EDGE,"E6.sketch_text.stroke-9"),sQuery(id+"F5.wireOp",EDGE,"E6.sketch_text.stroke-10"),sQuery(id+"F5.wireOp",EDGE,"E6.sketch_text.stroke-11"),sQuery(id+"F5.wireOp",EDGE,"E6.sketch_text.stroke-12"),sQuery(id+"F5.wireOp",EDGE,"E6.sketch_text.stroke-13"),sQuery(id+"F5.wireOp",EDGE,"E6.sketch_text.stroke-14"),sQuery(id+"F5.wireOp",EDGE,"E6.sketch_text.stroke-15")])]});
            var Q2;
            Q2=makeQuery(id+"F6.opExtrude","SWEPT_BODY",BODY,{"disambiguationData":[OSD([sQuery(id+"F5.wireOp",EDGE,"E5.sketch_text.stroke-0"),sQuery(id+"F5.wireOp",EDGE,"E5.sketch_text.stroke-1"),sQuery(id+"F5.wireOp",EDGE,"E5.sketch_text.stroke-2"),sQuery(id+"F5.wireOp",EDGE,"E5.sketch_text.stroke-3"),sQuery(id+"F5.wireOp",EDGE,"E5.sketch_text.stroke-4"),sQuery(id+"F5.wireOp",EDGE,"E5.sketch_text.stroke-5"),sQuery(id+"F5.wireOp",EDGE,"E5.sketch_text.stroke-6"),sQuery(id+"F5.wireOp",EDGE,"E5.sketch_text.stroke-7"),sQuery(id+"F5.wireOp",EDGE,"E5.sketch_text.stroke-8"),sQuery(id+"F5.wireOp",EDGE,"E5.sketch_text.stroke-9"),sQuery(id+"F5.wireOp",EDGE,"E5.sketch_text.stroke-10"),sQuery(id+"F5.wireOp",EDGE,"E5.sketch_text.stroke-11"),sQuery(id+"F5.wireOp",EDGE,"E5.sketch_text.stroke-12"),sQuery(id+"F5.wireOp",EDGE,"E5.sketch_text.stroke-13"),sQuery(id+"F5.wireOp",EDGE,"E5.sketch_text.stroke-14"),sQuery(id+"F5.wireOp",EDGE,"E5.sketch_text.stroke-15"),sQuery(id+"F5.wireOp",EDGE,"E5.sketch_text.stroke-16"),sQuery(id+"F5.wireOp",EDGE,"E5.sketch_text.stroke-17"),sQuery(id+"F5.wireOp",EDGE,"E5.sketch_text.stroke-18"),sQuery(id+"F5.wireOp",EDGE,"E5.sketch_text.stroke-19"),sQuery(id+"F5.wireOp",EDGE,"E5.sketch_text.stroke-20"),sQuery(id+"F5.wireOp",EDGE,"E5.sketch_text.stroke-21")])]});
            var Q3;
            Q3=makeQuery(id+"F6.opExtrude","SWEPT_BODY",BODY,{"disambiguationData":[OSD([sQuery(id+"F5.wireOp",EDGE,"E4.sketch_text.stroke-36"),sQuery(id+"F5.wireOp",EDGE,"E4.sketch_text.stroke-37"),sQuery(id+"F5.wireOp",EDGE,"E4.sketch_text.stroke-38"),sQuery(id+"F5.wireOp",EDGE,"E4.sketch_text.stroke-39"),sQuery(id+"F5.wireOp",EDGE,"E4.sketch_text.stroke-40"),sQuery(id+"F5.wireOp",EDGE,"E4.sketch_text.stroke-41"),sQuery(id+"F5.wireOp",EDGE,"E4.sketch_text.stroke-42"),sQuery(id+"F5.wireOp",EDGE,"E4.sketch_text.stroke-43"),sQuery(id+"F5.wireOp",EDGE,"E4.sketch_text.stroke-44"),sQuery(id+"F5.wireOp",EDGE,"E4.sketch_text.stroke-45"),sQuery(id+"F5.wireOp",EDGE,"E4.sketch_text.stroke-46"),sQuery(id+"F5.wireOp",EDGE,"E4.sketch_text.stroke-47"),sQuery(id+"F5.wireOp",EDGE,"E4.sketch_text.stroke-48"),sQuery(id+"F5.wireOp",EDGE,"E4.sketch_text.stroke-49"),sQuery(id+"F5.wireOp",EDGE,"E4.sketch_text.stroke-50"),sQuery(id+"F5.wireOp",EDGE,"E4.sketch_text.stroke-51"),sQuery(id+"F5.wireOp",EDGE,"E4.sketch_text.stroke-52"),sQuery(id+"F5.wireOp",EDGE,"E4.sketch_text.stroke-53"),sQuery(id+"F5.wireOp",EDGE,"E4.sketch_text.stroke-54"),sQuery(id+"F5.wireOp",EDGE,"E4.sketch_text.stroke-55"),sQuery(id+"F5.wireOp",EDGE,"E4.sketch_text.stroke-56"),sQuery(id+"F5.wireOp",EDGE,"E4.sketch_text.stroke-57"),sQuery(id+"F5.wireOp",EDGE,"E4.sketch_text.stroke-58"),sQuery(id+"F5.wireOp",EDGE,"E4.sketch_text.stroke-59"),sQuery(id+"F5.wireOp",EDGE,"E4.sketch_text.stroke-60"),sQuery(id+"F5.wireOp",EDGE,"E4.sketch_text.stroke-61"),sQuery(id+"F5.wireOp",EDGE,"E4.sketch_text.stroke-62"),sQuery(id+"F5.wireOp",EDGE,"E4.sketch_text.stroke-63"),sQuery(id+"F5.wireOp",EDGE,"E4.sketch_text.stroke-64"),sQuery(id+"F5.wireOp",EDGE,"E4.sketch_text.stroke-65"),sQuery(id+"F5.wireOp",EDGE,"E4.sketch_text.stroke-66"),sQuery(id+"F5.wireOp",EDGE,"E4.sketch_text.stroke-67")])]});
            var Q4;
            Q4=makeQuery(id+"F6.opExtrude","SWEPT_BODY",BODY,{"disambiguationData":[OSD([sQuery(id+"F5.wireOp",EDGE,"E4.sketch_text.stroke-32"),sQuery(id+"F5.wireOp",EDGE,"E4.sketch_text.stroke-33"),sQuery(id+"F5.wireOp",EDGE,"E4.sketch_text.stroke-34"),sQuery(id+"F5.wireOp",EDGE,"E4.sketch_text.stroke-35")])]});
            var Q5;
            Q5=makeQuery(id+"F6.opExtrude","SWEPT_BODY",BODY,{"disambiguationData":[OSD([sQuery(id+"F5.wireOp",EDGE,"E4.sketch_text.stroke-28"),sQuery(id+"F5.wireOp",EDGE,"E4.sketch_text.stroke-29"),sQuery(id+"F5.wireOp",EDGE,"E4.sketch_text.stroke-30"),sQuery(id+"F5.wireOp",EDGE,"E4.sketch_text.stroke-31")])]});
            var Q6;
            Q6=makeQuery(id+"F6.opExtrude","SWEPT_BODY",BODY,{"disambiguationData":[OSD([sQuery(id+"F5.wireOp",EDGE,"E4.sketch_text.stroke-24"),sQuery(id+"F5.wireOp",EDGE,"E4.sketch_text.stroke-25"),sQuery(id+"F5.wireOp",EDGE,"E4.sketch_text.stroke-26"),sQuery(id+"F5.wireOp",EDGE,"E4.sketch_text.stroke-27")])]});
            var Q7;
            Q7=makeQuery(id+"F6.opExtrude","SWEPT_BODY",BODY,{"disambiguationData":[OSD([sQuery(id+"F5.wireOp",EDGE,"E4.sketch_text.stroke-20"),sQuery(id+"F5.wireOp",EDGE,"E4.sketch_text.stroke-21"),sQuery(id+"F5.wireOp",EDGE,"E4.sketch_text.stroke-22"),sQuery(id+"F5.wireOp",EDGE,"E4.sketch_text.stroke-23")])]});
            var Q8;
            Q8=makeQuery(id+"F6.opExtrude","SWEPT_BODY",BODY,{"disambiguationData":[OSD([sQuery(id+"F5.wireOp",EDGE,"E4.sketch_text.stroke-0"),sQuery(id+"F5.wireOp",EDGE,"E4.sketch_text.stroke-1"),sQuery(id+"F5.wireOp",EDGE,"E4.sketch_text.stroke-2"),sQuery(id+"F5.wireOp",EDGE,"E4.sketch_text.stroke-3"),sQuery(id+"F5.wireOp",EDGE,"E4.sketch_text.stroke-4"),sQuery(id+"F5.wireOp",EDGE,"E4.sketch_text.stroke-5"),sQuery(id+"F5.wireOp",EDGE,"E4.sketch_text.stroke-6"),sQuery(id+"F5.wireOp",EDGE,"E4.sketch_text.stroke-7"),sQuery(id+"F5.wireOp",EDGE,"E4.sketch_text.stroke-8"),sQuery(id+"F5.wireOp",EDGE,"E4.sketch_text.stroke-9"),sQuery(id+"F5.wireOp",EDGE,"E4.sketch_text.stroke-10"),sQuery(id+"F5.wireOp",EDGE,"E4.sketch_text.stroke-11"),sQuery(id+"F5.wireOp",EDGE,"E4.sketch_text.stroke-12"),sQuery(id+"F5.wireOp",EDGE,"E4.sketch_text.stroke-13"),sQuery(id+"F5.wireOp",EDGE,"E4.sketch_text.stroke-14"),sQuery(id+"F5.wireOp",EDGE,"E4.sketch_text.stroke-15"),sQuery(id+"F5.wireOp",EDGE,"E4.sketch_text.stroke-16"),sQuery(id+"F5.wireOp",EDGE,"E4.sketch_text.stroke-17"),sQuery(id+"F5.wireOp",EDGE,"E4.sketch_text.stroke-18"),sQuery(id+"F5.wireOp",EDGE,"E4.sketch_text.stroke-19")])]});
            var Q9;
            Q9=makeQuery(id+"F6.opExtrude","SWEPT_BODY",BODY,{"disambiguationData":[OSD([sQuery(id+"F5.wireOp",EDGE,"E3.sketch_text.stroke-52"),sQuery(id+"F5.wireOp",EDGE,"E3.sketch_text.stroke-53"),sQuery(id+"F5.wireOp",EDGE,"E3.sketch_text.stroke-54"),sQuery(id+"F5.wireOp",EDGE,"E3.sketch_text.stroke-55")])]});
            var Q10;
            Q10=makeQuery(id+"F6.opExtrude","SWEPT_BODY",BODY,{"disambiguationData":[OSD([sQuery(id+"F5.wireOp",EDGE,"E3.sketch_text.stroke-44"),sQuery(id+"F5.wireOp",EDGE,"E3.sketch_text.stroke-45"),sQuery(id+"F5.wireOp",EDGE,"E3.sketch_text.stroke-46"),sQuery(id+"F5.wireOp",EDGE,"E3.sketch_text.stroke-47"),sQuery(id+"F5.wireOp",EDGE,"E3.sketch_text.stroke-48"),sQuery(id+"F5.wireOp",EDGE,"E3.sketch_text.stroke-49"),sQuery(id+"F5.wireOp",EDGE,"E3.sketch_text.stroke-50"),sQuery(id+"F5.wireOp",EDGE,"E3.sketch_text.stroke-51")])]});
            var Q11;
            Q11=makeQuery(id+"F6.opExtrude","SWEPT_BODY",BODY,{"disambiguationData":[OSD([sQuery(id+"F5.wireOp",EDGE,"E3.sketch_text.stroke-4"),sQuery(id+"F5.wireOp",EDGE,"E3.sketch_text.stroke-5"),sQuery(id+"F5.wireOp",EDGE,"E3.sketch_text.stroke-6"),sQuery(id+"F5.wireOp",EDGE,"E3.sketch_text.stroke-7"),sQuery(id+"F5.wireOp",EDGE,"E3.sketch_text.stroke-8"),sQuery(id+"F5.wireOp",EDGE,"E3.sketch_text.stroke-9"),sQuery(id+"F5.wireOp",EDGE,"E3.sketch_text.stroke-10"),sQuery(id+"F5.wireOp",EDGE,"E3.sketch_text.stroke-11"),sQuery(id+"F5.wireOp",EDGE,"E3.sketch_text.stroke-12"),sQuery(id+"F5.wireOp",EDGE,"E3.sketch_text.stroke-13"),sQuery(id+"F5.wireOp",EDGE,"E3.sketch_text.stroke-14"),sQuery(id+"F5.wireOp",EDGE,"E3.sketch_text.stroke-15"),sQuery(id+"F5.wireOp",EDGE,"E3.sketch_text.stroke-16"),sQuery(id+"F5.wireOp",EDGE,"E3.sketch_text.stroke-17"),sQuery(id+"F5.wireOp",EDGE,"E3.sketch_text.stroke-18"),sQuery(id+"F5.wireOp",EDGE,"E3.sketch_text.stroke-19"),sQuery(id+"F5.wireOp",EDGE,"E3.sketch_text.stroke-20"),sQuery(id+"F5.wireOp",EDGE,"E3.sketch_text.stroke-21"),sQuery(id+"F5.wireOp",EDGE,"E3.sketch_text.stroke-22"),sQuery(id+"F5.wireOp",EDGE,"E3.sketch_text.stroke-23"),sQuery(id+"F5.wireOp",EDGE,"E3.sketch_text.stroke-24"),sQuery(id+"F5.wireOp",EDGE,"E3.sketch_text.stroke-25"),sQuery(id+"F5.wireOp",EDGE,"E3.sketch_text.stroke-26"),sQuery(id+"F5.wireOp",EDGE,"E3.sketch_text.stroke-27"),sQuery(id+"F5.wireOp",EDGE,"E3.sketch_text.stroke-28"),sQuery(id+"F5.wireOp",EDGE,"E3.sketch_text.stroke-29"),sQuery(id+"F5.wireOp",EDGE,"E3.sketch_text.stroke-30"),sQuery(id+"F5.wireOp",EDGE,"E3.sketch_text.stroke-31"),sQuery(id+"F5.wireOp",EDGE,"E3.sketch_text.stroke-32"),sQuery(id+"F5.wireOp",EDGE,"E3.sketch_text.stroke-33"),sQuery(id+"F5.wireOp",EDGE,"E3.sketch_text.stroke-34"),sQuery(id+"F5.wireOp",EDGE,"E3.sketch_text.stroke-35"),sQuery(id+"F5.wireOp",EDGE,"E3.sketch_text.stroke-36"),sQuery(id+"F5.wireOp",EDGE,"E3.sketch_text.stroke-37"),sQuery(id+"F5.wireOp",EDGE,"E3.sketch_text.stroke-38"),sQuery(id+"F5.wireOp",EDGE,"E3.sketch_text.stroke-39"),sQuery(id+"F5.wireOp",EDGE,"E3.sketch_text.stroke-40"),sQuery(id+"F5.wireOp",EDGE,"E3.sketch_text.stroke-41"),sQuery(id+"F5.wireOp",EDGE,"E3.sketch_text.stroke-42"),sQuery(id+"F5.wireOp",EDGE,"E3.sketch_text.stroke-43")])]});
            var Q12;
            Q12=makeQuery(id+"F6.opExtrude","SWEPT_BODY",BODY,{"disambiguationData":[OSD([sQuery(id+"F5.wireOp",EDGE,"E3.sketch_text.stroke-0"),sQuery(id+"F5.wireOp",EDGE,"E3.sketch_text.stroke-1"),sQuery(id+"F5.wireOp",EDGE,"E3.sketch_text.stroke-2"),sQuery(id+"F5.wireOp",EDGE,"E3.sketch_text.stroke-3")])]});
            var Q13;
            Q13=makeQuery(id+"F6.opExtrude","SWEPT_BODY",BODY,{"disambiguationData":[OSD([sQuery(id+"F5.wireOp",EDGE,"E2.sketch_text.stroke-19"),sQuery(id+"F5.wireOp",EDGE,"E2.sketch_text.stroke-20"),sQuery(id+"F5.wireOp",EDGE,"E2.sketch_text.stroke-21"),sQuery(id+"F5.wireOp",EDGE,"E2.sketch_text.stroke-22"),sQuery(id+"F5.wireOp",EDGE,"E2.sketch_text.stroke-23"),sQuery(id+"F5.wireOp",EDGE,"E2.sketch_text.stroke-24"),sQuery(id+"F5.wireOp",EDGE,"E2.sketch_text.stroke-25"),sQuery(id+"F5.wireOp",EDGE,"E2.sketch_text.stroke-26"),sQuery(id+"F5.wireOp",EDGE,"E2.sketch_text.stroke-27"),sQuery(id+"F5.wireOp",EDGE,"E2.sketch_text.stroke-28"),sQuery(id+"F5.wireOp",EDGE,"E2.sketch_text.stroke-29"),sQuery(id+"F5.wireOp",EDGE,"E2.sketch_text.stroke-30"),sQuery(id+"F5.wireOp",EDGE,"E2.sketch_text.stroke-31"),sQuery(id+"F5.wireOp",EDGE,"E2.sketch_text.stroke-32"),sQuery(id+"F5.wireOp",EDGE,"E2.sketch_text.stroke-33")])]});
            var Q14;
            Q14=makeQuery(id+"F6.opExtrude","SWEPT_BODY",BODY,{"disambiguationData":[OSD([sQuery(id+"F5.wireOp",EDGE,"E2.sketch_text.stroke-4"),sQuery(id+"F5.wireOp",EDGE,"E2.sketch_text.stroke-5"),sQuery(id+"F5.wireOp",EDGE,"E2.sketch_text.stroke-6"),sQuery(id+"F5.wireOp",EDGE,"E2.sketch_text.stroke-7"),sQuery(id+"F5.wireOp",EDGE,"E2.sketch_text.stroke-8"),sQuery(id+"F5.wireOp",EDGE,"E2.sketch_text.stroke-9"),sQuery(id+"F5.wireOp",EDGE,"E2.sketch_text.stroke-10"),sQuery(id+"F5.wireOp",EDGE,"E2.sketch_text.stroke-11"),sQuery(id+"F5.wireOp",EDGE,"E2.sketch_text.stroke-12"),sQuery(id+"F5.wireOp",EDGE,"E2.sketch_text.stroke-13"),sQuery(id+"F5.wireOp",EDGE,"E2.sketch_text.stroke-14"),sQuery(id+"F5.wireOp",EDGE,"E2.sketch_text.stroke-15"),sQuery(id+"F5.wireOp",EDGE,"E2.sketch_text.stroke-16"),sQuery(id+"F5.wireOp",EDGE,"E2.sketch_text.stroke-17"),sQuery(id+"F5.wireOp",EDGE,"E2.sketch_text.stroke-18")])]});
            var Q15;
            Q15=makeQuery(id+"F6.opExtrude","SWEPT_BODY",BODY,{"disambiguationData":[OSD([sQuery(id+"F5.wireOp",EDGE,"E2.sketch_text.stroke-0"),sQuery(id+"F5.wireOp",EDGE,"E2.sketch_text.stroke-1"),sQuery(id+"F5.wireOp",EDGE,"E2.sketch_text.stroke-2"),sQuery(id+"F5.wireOp",EDGE,"E2.sketch_text.stroke-3")])]});
            var Q16;
            Q16=makeQuery(id+"F1.opExtrude","SWEPT_BODY",BODY,{"disambiguationData":[OSD([sQuery(id+"F0.wireOp",EDGE,"E0")])]});
            booleanBodies(context, id + "F18", {"operationType" : BooleanOperationType.SUBTRACTION, "tools" : qUnion([Q0, Q1, Q2, Q3, Q4, Q5, Q6, Q7, Q8, Q9, Q10, Q11, Q12, Q13, Q14, Q15]), "targets" : qUnion([Q16])});
        }
    });
